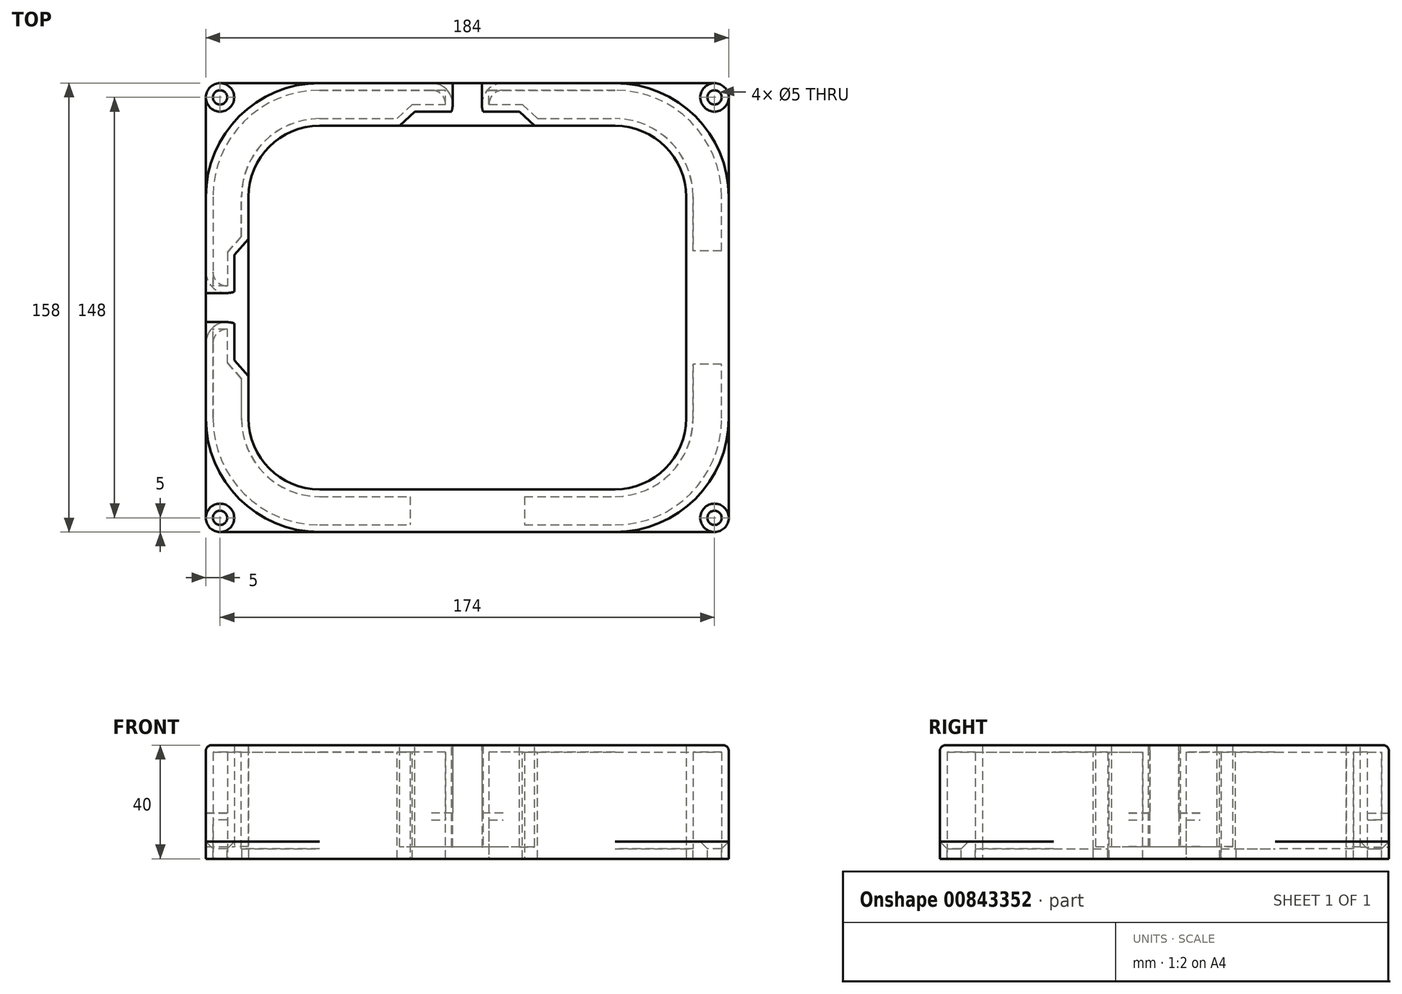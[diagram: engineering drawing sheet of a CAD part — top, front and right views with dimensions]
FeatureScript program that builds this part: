
annotation { "Feature Type Name" : "Feature", "Feature Type Description" : "" }
export const myFeature = defineFeature(function(context is Context, id is Id, definition is map)
    precondition{}
    {
        {
            var Q0;
            Q0=qCreatedBy(makeId("Top.planeOp"),FACE);
            var sketch = newSketch(context, id + "F0", { "sketchPlane" : qUnion([Q0])});
            skLineSegment(sketch, "E0.bottom", {"start": v(-51.5, 63.5) * mm, "end": v(51.5, 63.5) * mm});
            skLineSegment(sketch, "E0.top", {"start": v(-51.5, -63.5) * mm, "end": v(51.5, -63.5) * mm});
            skLineSegment(sketch, "E0.left", {"start": v(-76.5, 38.5) * mm, "end": v(-76.5, -38.5) * mm});
            skLineSegment(sketch, "E0.right", {"start": v(76.5, 38.5) * mm, "end": v(76.5, -38.5) * mm});
            skPoint(sketch, "E0.middle", {"position": v(0, 0) * mm});
            skPoint(sketch, "E1.visualSharp", {"position": v(-76.5, 63.5) * mm});
            skArc(sketch, "E1.filletArc", {"start": v(-51.5, 63.5) * mm, "mid": v(-69.18, 56.18) * mm, "end": v(-76.5, 38.5) * mm});
            skPoint(sketch, "E2.visualSharp", {"position": v(76.5, -63.5) * mm});
            skArc(sketch, "E2.filletArc", {"start": v(51.5, -63.5) * mm, "mid": v(69.18, -56.18) * mm, "end": v(76.5, -38.5) * mm});
            skPoint(sketch, "E3.visualSharp", {"position": v(76.5, 63.5) * mm});
            skArc(sketch, "E3.filletArc", {"start": v(76.5, 38.5) * mm, "mid": v(69.18, 56.18) * mm, "end": v(51.5, 63.5) * mm});
            skPoint(sketch, "E4.visualSharp", {"position": v(-76.5, -63.5) * mm});
            skArc(sketch, "E4.filletArc", {"start": v(-76.5, -38.5) * mm, "mid": v(-69.18, -56.18) * mm, "end": v(-51.5, -63.5) * mm});
            skSolve(sketch);
        }
        {
            var Q0;
            Q0 = qSketchRegion(id + "F0", true);
            extrude(context, id + "F1", {"entities" : qUnion([Q0]), "depth" : 5 * mm, "offsetDistance" : 25 * mm});
        }
        {
            var Q0;
            Q0=qCreatedBy(makeId("Top.planeOp"),FACE);
            var sketch = newSketch(context, id + "F2", { "sketchPlane" : qUnion([Q0])});
            skLineSegment(sketch, "E5.bottom", {"start": v(-52, 64) * mm, "end": v(52, 64) * mm});
            skLineSegment(sketch, "E5.top", {"start": v(-52, -64) * mm, "end": v(52, -64) * mm});
            skLineSegment(sketch, "E5.left", {"start": v(-77, 39) * mm, "end": v(-77, -39) * mm});
            skLineSegment(sketch, "E5.right", {"start": v(77, 39) * mm, "end": v(77, -39) * mm});
            skPoint(sketch, "E5.middle", {"position": v(0, 0) * mm});
            skPoint(sketch, "E6.visualSharp", {"position": v(-77, 64) * mm});
            skArc(sketch, "E6.filletArc", {"start": v(-52, 64) * mm, "mid": v(-69.68, 56.68) * mm, "end": v(-77, 39) * mm});
            skPoint(sketch, "E7.visualSharp", {"position": v(77, 64) * mm});
            skArc(sketch, "E7.filletArc", {"start": v(77, 39) * mm, "mid": v(69.68, 56.68) * mm, "end": v(52, 64) * mm});
            skPoint(sketch, "E8.visualSharp", {"position": v(77, -64) * mm});
            skArc(sketch, "E8.filletArc", {"start": v(52, -64) * mm, "mid": v(69.68, -56.68) * mm, "end": v(77, -39) * mm});
            skPoint(sketch, "E9.visualSharp", {"position": v(-77, -64) * mm});
            skArc(sketch, "E9.filletArc", {"start": v(-77, -39) * mm, "mid": v(-69.68, -56.68) * mm, "end": v(-52, -64) * mm});
            skArc(sketch, "E10.0", {"start": v(-52, 79) * mm, "mid": v(-80.28, 67.28) * mm, "end": v(-92, 39) * mm});
            skLineSegment(sketch, "E10.1", {"start": v(-92, 39) * mm, "end": v(-92, -39) * mm});
            skLineSegment(sketch, "E10.2", {"start": v(-52, 79) * mm, "end": v(52, 79) * mm});
            skArc(sketch, "E10.3", {"start": v(-92, -39) * mm, "mid": v(-80.28, -67.28) * mm, "end": v(-52, -79) * mm});
            skArc(sketch, "E10.4", {"start": v(92, 39) * mm, "mid": v(80.28, 67.28) * mm, "end": v(52, 79) * mm});
            skLineSegment(sketch, "E10.5", {"start": v(92, 39) * mm, "end": v(92, -39) * mm});
            skArc(sketch, "E10.6", {"start": v(52, -79) * mm, "mid": v(80.28, -67.28) * mm, "end": v(92, -39) * mm});
            skLineSegment(sketch, "E10.7", {"start": v(-52, -79) * mm, "end": v(52, -79) * mm});
            skSolve(sketch);
        }
        {
            var Q0;
            Q0 = qSketchRegion(id + "F2", true);
            extrude(context, id + "F3", {"entities" : qUnion([Q0]), "depth" : 40 * mm, "offsetDistance" : 25 * mm});
        }
        {
            var Q0;
            Q0=makeQuery(id+"F3.opExtrude","CAP_FACE",FACE,{"disambiguationData":[OSD([sQuery(id+"F2.wireOp",EDGE,"E5.bottom"),sQuery(id+"F2.wireOp",EDGE,"E5.top"),sQuery(id+"F2.wireOp",EDGE,"E5.left"),sQuery(id+"F2.wireOp",EDGE,"E5.right"),sQuery(id+"F2.wireOp",EDGE,"E6.filletArc"),sQuery(id+"F2.wireOp",EDGE,"E7.filletArc"),sQuery(id+"F2.wireOp",EDGE,"E8.filletArc"),sQuery(id+"F2.wireOp",EDGE,"E9.filletArc"),sQuery(id+"F2.wireOp",EDGE,"E10.0"),sQuery(id+"F2.wireOp",EDGE,"E10.1"),sQuery(id+"F2.wireOp",EDGE,"E10.2"),sQuery(id+"F2.wireOp",EDGE,"E10.3"),sQuery(id+"F2.wireOp",EDGE,"E10.4"),sQuery(id+"F2.wireOp",EDGE,"E10.5"),sQuery(id+"F2.wireOp",EDGE,"E10.6"),sQuery(id+"F2.wireOp",EDGE,"E10.7")])],"isStart":true});
            var sketch = newSketch(context, id + "F4", { "sketchPlane" : qUnion([Q0])});
            skLineSegment(sketch, "E11.bottom", {"start": v(-87, 79) * mm, "end": v(87, 79) * mm});
            skLineSegment(sketch, "E11.top", {"start": v(-87, -79) * mm, "end": v(87, -79) * mm});
            skLineSegment(sketch, "E11.left", {"start": v(-92, 74) * mm, "end": v(-92, -74) * mm});
            skLineSegment(sketch, "E11.right", {"start": v(92, 74) * mm, "end": v(92, -74) * mm});
            skPoint(sketch, "E11.middle", {"position": v(0, 0) * mm});
            skPoint(sketch, "E12.visualSharp", {"position": v(-92, 79) * mm});
            skArc(sketch, "E12.filletArc", {"start": v(-87, 79) * mm, "mid": v(-90.54, 77.54) * mm, "end": v(-92, 74) * mm});
            skPoint(sketch, "E13.visualSharp", {"position": v(92, 79) * mm});
            skArc(sketch, "E13.filletArc", {"start": v(92, 74) * mm, "mid": v(90.54, 77.54) * mm, "end": v(87, 79) * mm});
            skPoint(sketch, "E14.visualSharp", {"position": v(92, -79) * mm});
            skArc(sketch, "E14.filletArc", {"start": v(87, -79) * mm, "mid": v(90.54, -77.54) * mm, "end": v(92, -74) * mm});
            skPoint(sketch, "E15.visualSharp", {"position": v(-92, -79) * mm});
            skArc(sketch, "E15.filletArc", {"start": v(-92, -74) * mm, "mid": v(-90.54, -77.54) * mm, "end": v(-87, -79) * mm});
            skLineSegment(sketch, "E16.bottom", {"start": v(-51.94, 64) * mm, "end": v(51.94, 64) * mm});
            skLineSegment(sketch, "E16.top", {"start": v(-51.94, -64) * mm, "end": v(51.94, -64) * mm});
            skLineSegment(sketch, "E16.left", {"start": v(-76.94, 39) * mm, "end": v(-76.94, -39) * mm});
            skLineSegment(sketch, "E16.right", {"start": v(76.94, 39) * mm, "end": v(76.94, -39) * mm});
            skPoint(sketch, "E17.visualSharp", {"position": v(-76.94, 64) * mm});
            skArc(sketch, "E17.filletArc", {"start": v(-51.94, 64) * mm, "mid": v(-69.61, 56.68) * mm, "end": v(-76.94, 39) * mm});
            skPoint(sketch, "E18.visualSharp", {"position": v(76.94, 64) * mm});
            skArc(sketch, "E18.filletArc", {"start": v(76.94, 39) * mm, "mid": v(69.61, 56.68) * mm, "end": v(51.94, 64) * mm});
            skPoint(sketch, "E19.visualSharp", {"position": v(-76.94, -64) * mm});
            skArc(sketch, "E19.filletArc", {"start": v(-76.94, -39) * mm, "mid": v(-69.61, -56.68) * mm, "end": v(-51.94, -64) * mm});
            skPoint(sketch, "E20.visualSharp", {"position": v(76.94, -64) * mm});
            skArc(sketch, "E20.filletArc", {"start": v(51.94, -64) * mm, "mid": v(69.61, -56.68) * mm, "end": v(76.94, -39) * mm});
            skSolve(sketch);
        }
        {
            var Q0;
            Q0 = qSketchRegion(id + "F4", true);
            extrude(context, id + "F5", {"entities" : qUnion([Q0]), "oppositeDirection" : true, "depth" : 6 * mm, "offsetDistance" : 25 * mm});
        }
        {
            var Q0;
            Q0=makeQuery(id+"F5.opExtrude","CAP_FACE",FACE,{"disambiguationData":[OSD([sQuery(id+"F4.wireOp",EDGE,"E11.bottom"),sQuery(id+"F4.wireOp",EDGE,"E11.top"),sQuery(id+"F4.wireOp",EDGE,"E11.left"),sQuery(id+"F4.wireOp",EDGE,"E11.right"),sQuery(id+"F4.wireOp",EDGE,"E12.filletArc"),sQuery(id+"F4.wireOp",EDGE,"E13.filletArc"),sQuery(id+"F4.wireOp",EDGE,"E14.filletArc"),sQuery(id+"F4.wireOp",EDGE,"E15.filletArc"),sQuery(id+"F4.wireOp",EDGE,"E16.bottom"),sQuery(id+"F4.wireOp",EDGE,"E16.top"),sQuery(id+"F4.wireOp",EDGE,"E16.left"),sQuery(id+"F4.wireOp",EDGE,"E16.right"),sQuery(id+"F4.wireOp",EDGE,"E17.filletArc"),sQuery(id+"F4.wireOp",EDGE,"E18.filletArc"),sQuery(id+"F4.wireOp",EDGE,"E19.filletArc"),sQuery(id+"F4.wireOp",EDGE,"E20.filletArc")])],"isStart":false});
            var sketch = newSketch(context, id + "F6", { "sketchPlane" : qUnion([Q0])});
            skPoint(sketch, "E21", {"position": v(-87, -74) * mm});
            skPoint(sketch, "E22", {"position": v(-87, 74) * mm});
            skPoint(sketch, "E23", {"position": v(87, 74) * mm});
            skPoint(sketch, "E24", {"position": v(87, -74) * mm});
            skSolve(sketch);
        }
        {
            var Q0;
            Q0=sQuery(id+"F6.wireOp",VERTEX,"E24");
            var Q1;
            Q1=sQuery(id+"F6.wireOp",VERTEX,"E21");
            var Q2;
            Q2=sQuery(id+"F6.wireOp",VERTEX,"E22");
            var Q3;
            Q3=sQuery(id+"F6.wireOp",VERTEX,"E23");
            var Q4;
            Q4=makeQuery(id+"F5.opExtrude","SWEPT_BODY",BODY,{"disambiguationData":[OSD([sQuery(id+"F4.wireOp",EDGE,"E11.bottom"),sQuery(id+"F4.wireOp",EDGE,"E11.top"),sQuery(id+"F4.wireOp",EDGE,"E11.left"),sQuery(id+"F4.wireOp",EDGE,"E11.right"),sQuery(id+"F4.wireOp",EDGE,"E12.filletArc"),sQuery(id+"F4.wireOp",EDGE,"E13.filletArc"),sQuery(id+"F4.wireOp",EDGE,"E14.filletArc"),sQuery(id+"F4.wireOp",EDGE,"E15.filletArc"),sQuery(id+"F4.wireOp",EDGE,"E16.bottom"),sQuery(id+"F4.wireOp",EDGE,"E16.top"),sQuery(id+"F4.wireOp",EDGE,"E16.left"),sQuery(id+"F4.wireOp",EDGE,"E16.right"),sQuery(id+"F4.wireOp",EDGE,"E17.filletArc"),sQuery(id+"F4.wireOp",EDGE,"E18.filletArc"),sQuery(id+"F4.wireOp",EDGE,"E19.filletArc"),sQuery(id+"F4.wireOp",EDGE,"E20.filletArc")])]});
            hole(context, id + "F7", {"style" : HoleStyle.C_SINK, "endStyle" : HoleEndStyle.THROUGH, "standardTappedOrClearance" : lookupTablePath({ "standard" : "ISO", "size" : "5", "type" : "Drilled" }), "standardBlindInLast" : lookupTablePath({ "standard" : "ISO", "size" : "5", "type" : "Drilled" }), "holeDiameter" : 5 * mm, "cSinkDiameter" : 10 * mm, "cSinkAngle" : 90 * degree, "majorDiameter" : 5 * mm, "isTappedThrough" : true, "tappedDepth" : 12 * mm, "tapClearance" : 3, "locations" : qUnion([Q0, Q1, Q2, Q3]), "scope" : qUnion([Q4])});
        }
        {
            var Q0;
            Q0=makeQuery(id+"F3.opExtrude","SWEPT_FACE",FACE,{"disambiguationData":[OSD([sQuery(id+"F2.wireOp",EDGE,"E10.1")])]});
            var sketch = newSketch(context, id + "F8", { "sketchPlane" : qUnion([Q0])});
            skLineSegment(sketch, "E25", {"start": v(0, 40) * mm, "end": v(0, 16.12) * mm});
            skLineSegment(sketch, "E26.bottom", {"start": v(-5.13, 40) * mm, "end": v(5.13, 40) * mm});
            skLineSegment(sketch, "E26.top", {"start": v(-5.13, 16.12) * mm, "end": v(5.13, 16.12) * mm});
            skLineSegment(sketch, "E26.left", {"start": v(-5.13, 40) * mm, "end": v(-5.13, 16.12) * mm});
            skLineSegment(sketch, "E26.right", {"start": v(5.13, 40) * mm, "end": v(5.13, 16.12) * mm});
            skPoint(sketch, "E26.middle", {"position": v(0, 28.06) * mm});
            skSolve(sketch);
        }
        {
            var Q0;
            Q0 = qSketchRegion(id + "F8", true);
            extrude(context, id + "F9", {"entities" : qUnion([Q0]), "operationType" : NewBodyOperationType.REMOVE, "oppositeDirection" : true, "depth" : 25 * mm, "offsetDistance" : 25 * mm});
        }
        {
            var Q0;
            Q0=makeQuery(id+"F3.opExtrude","SWEPT_FACE",FACE,{"disambiguationData":[OSD([sQuery(id+"F2.wireOp",EDGE,"E10.2")])]});
            var sketch = newSketch(context, id + "F10", { "sketchPlane" : qUnion([Q0])});
            skLineSegment(sketch, "E27", {"start": v(0, 40) * mm, "end": v(0, 16.14) * mm});
            skLineSegment(sketch, "E28.bottom", {"start": v(-5.13, 40) * mm, "end": v(5.13, 40) * mm});
            skLineSegment(sketch, "E28.top", {"start": v(-5.13, 16.14) * mm, "end": v(5.13, 16.14) * mm});
            skLineSegment(sketch, "E28.left", {"start": v(-5.13, 40) * mm, "end": v(-5.13, 16.14) * mm});
            skLineSegment(sketch, "E28.right", {"start": v(5.13, 40) * mm, "end": v(5.13, 16.14) * mm});
            skPoint(sketch, "E28.middle", {"position": v(0, 28.07) * mm});
            skSolve(sketch);
        }
        {
            var Q0;
            Q0 = qSketchRegion(id + "F10", true);
            extrude(context, id + "F11", {"entities" : qUnion([Q0]), "operationType" : NewBodyOperationType.REMOVE, "oppositeDirection" : true, "depth" : 25 * mm, "offsetDistance" : 25 * mm});
        }
        {
            var Q0;
            Q0=makeQuery(id+"F11.boolean.opBoolean","INTERSECT",EDGE,{"derivedFrom":[makeQuery(id+"F3.opExtrude","SWEPT_FACE",FACE,{"disambiguationData":[OSD([sQuery(id+"F2.wireOp",EDGE,"E5.bottom")])]}),makeQuery(id+"F11.opExtrude","SWEPT_FACE",FACE,{"disambiguationData":[OSD([sQuery(id+"F10.wireOp",EDGE,"E28.left")])]})]});
            var Q1;
            Q1=makeQuery(id+"F11.boolean.opBoolean","COPY",EDGE,{"derivedFrom":makeQuery(id+"F11.opExtrude","CAP_EDGE",EDGE,{"disambiguationData":[OSD([sQuery(id+"F10.wireOp",EDGE,"E28.left")])],"isStart":true})});
            var Q2;
            Q2=makeQuery(id+"F11.boolean.opBoolean","COPY",EDGE,{"derivedFrom":makeQuery(id+"F11.opExtrude","CAP_EDGE",EDGE,{"disambiguationData":[OSD([sQuery(id+"F10.wireOp",EDGE,"E28.right")])],"isStart":true})});
            var Q3;
            Q3=makeQuery(id+"F11.boolean.opBoolean","INTERSECT",EDGE,{"derivedFrom":[makeQuery(id+"F3.opExtrude","SWEPT_FACE",FACE,{"disambiguationData":[OSD([sQuery(id+"F2.wireOp",EDGE,"E5.bottom")])]}),makeQuery(id+"F11.opExtrude","SWEPT_FACE",FACE,{"disambiguationData":[OSD([sQuery(id+"F10.wireOp",EDGE,"E28.right")])]})]});
            var Q4;
            Q4=makeQuery(id+"F9.boolean.opBoolean","INTERSECT",EDGE,{"derivedFrom":[makeQuery(id+"F3.opExtrude","SWEPT_FACE",FACE,{"disambiguationData":[OSD([sQuery(id+"F2.wireOp",EDGE,"E5.left")])]}),makeQuery(id+"F9.opExtrude","SWEPT_FACE",FACE,{"disambiguationData":[OSD([sQuery(id+"F8.wireOp",EDGE,"E26.right")])]})]});
            var Q5;
            Q5=makeQuery(id+"F9.boolean.opBoolean","INTERSECT",EDGE,{"derivedFrom":[makeQuery(id+"F3.opExtrude","SWEPT_FACE",FACE,{"disambiguationData":[OSD([sQuery(id+"F2.wireOp",EDGE,"E5.left")])]}),makeQuery(id+"F9.opExtrude","SWEPT_FACE",FACE,{"disambiguationData":[OSD([sQuery(id+"F8.wireOp",EDGE,"E26.left")])]})]});
            var Q6;
            Q6=makeQuery(id+"F9.boolean.opBoolean","COPY",EDGE,{"derivedFrom":makeQuery(id+"F9.opExtrude","CAP_EDGE",EDGE,{"disambiguationData":[OSD([sQuery(id+"F8.wireOp",EDGE,"E26.right")])],"isStart":true})});
            var Q7;
            Q7=makeQuery(id+"F9.boolean.opBoolean","COPY",EDGE,{"derivedFrom":makeQuery(id+"F9.opExtrude","CAP_EDGE",EDGE,{"disambiguationData":[OSD([sQuery(id+"F8.wireOp",EDGE,"E26.left")])],"isStart":true})});
            fillet(context, id + "F12", {"entities" : qUnion([Q0, Q1, Q2, Q3, Q4, Q5, Q6, Q7]), "radius" : 7.5 * mm, "tangentPropagation" : true, "allowEdgeOverflow" : false});
        }
        {
            var Q0;
            Q0=makeQuery(id+"F3.opExtrude","CAP_EDGE",EDGE,{"disambiguationData":[OSD([sQuery(id+"F2.wireOp",EDGE,"E10.0")])],"isStart":false});
            var Q1;
            Q1=makeQuery(id+"F3.opExtrude","CAP_EDGE",EDGE,{"disambiguationData":[OSD([sQuery(id+"F2.wireOp",EDGE,"E10.4")])],"isStart":false});
            fillet(context, id + "F13", {"entities" : qUnion([Q0, Q1]), "radius" : 2 * mm, "tangentPropagation" : true, "allowEdgeOverflow" : false});
        }
        {
            var Q0;
            Q0=makeQuery(id+"F1.opExtrude","SWEPT_BODY",BODY,{"disambiguationData":[OSD([sQuery(id+"F0.wireOp",EDGE,"E0.bottom"),sQuery(id+"F0.wireOp",EDGE,"E0.top"),sQuery(id+"F0.wireOp",EDGE,"E0.left"),sQuery(id+"F0.wireOp",EDGE,"E0.right"),sQuery(id+"F0.wireOp",EDGE,"E1.filletArc"),sQuery(id+"F0.wireOp",EDGE,"E2.filletArc"),sQuery(id+"F0.wireOp",EDGE,"E3.filletArc"),sQuery(id+"F0.wireOp",EDGE,"E4.filletArc")])]});
            deleteBodies(context, id + "F14", {"entities" : qUnion([Q0])});
        }
        {
            var Q0;
            Q0=makeQuery(id+"F3.opExtrude","SWEPT_BODY",BODY,{"disambiguationData":[OSD([sQuery(id+"F2.wireOp",EDGE,"E5.bottom"),sQuery(id+"F2.wireOp",EDGE,"E5.top"),sQuery(id+"F2.wireOp",EDGE,"E5.left"),sQuery(id+"F2.wireOp",EDGE,"E5.right"),sQuery(id+"F2.wireOp",EDGE,"E6.filletArc"),sQuery(id+"F2.wireOp",EDGE,"E7.filletArc"),sQuery(id+"F2.wireOp",EDGE,"E8.filletArc"),sQuery(id+"F2.wireOp",EDGE,"E9.filletArc"),sQuery(id+"F2.wireOp",EDGE,"E10.0"),sQuery(id+"F2.wireOp",EDGE,"E10.1"),sQuery(id+"F2.wireOp",EDGE,"E10.2"),sQuery(id+"F2.wireOp",EDGE,"E10.3"),sQuery(id+"F2.wireOp",EDGE,"E10.4"),sQuery(id+"F2.wireOp",EDGE,"E10.5"),sQuery(id+"F2.wireOp",EDGE,"E10.6"),sQuery(id+"F2.wireOp",EDGE,"E10.7")])]});
            var Q1;
            Q1=makeQuery(id+"F5.opExtrude","SWEPT_BODY",BODY,{"disambiguationData":[OSD([sQuery(id+"F4.wireOp",EDGE,"E11.bottom"),sQuery(id+"F4.wireOp",EDGE,"E11.top"),sQuery(id+"F4.wireOp",EDGE,"E11.left"),sQuery(id+"F4.wireOp",EDGE,"E11.right"),sQuery(id+"F4.wireOp",EDGE,"E12.filletArc"),sQuery(id+"F4.wireOp",EDGE,"E13.filletArc"),sQuery(id+"F4.wireOp",EDGE,"E14.filletArc"),sQuery(id+"F4.wireOp",EDGE,"E15.filletArc"),sQuery(id+"F4.wireOp",EDGE,"E16.bottom"),sQuery(id+"F4.wireOp",EDGE,"E16.top"),sQuery(id+"F4.wireOp",EDGE,"E16.left"),sQuery(id+"F4.wireOp",EDGE,"E16.right"),sQuery(id+"F4.wireOp",EDGE,"E17.filletArc"),sQuery(id+"F4.wireOp",EDGE,"E18.filletArc"),sQuery(id+"F4.wireOp",EDGE,"E19.filletArc"),sQuery(id+"F4.wireOp",EDGE,"E20.filletArc")])]});
            booleanBodies(context, id + "F15", {"operationType" : BooleanOperationType.UNION, "tools" : qUnion([Q0, Q1])});
        }
        {
            var Q0;
            {var subQ0=sQuery(id+"F2.wireOp",EDGE,"E10.3");var subQ1=sQuery(id+"F2.wireOp",EDGE,"E10.2");var subQ2=sQuery(id+"F2.wireOp",EDGE,"E9.filletArc");var subQ3=sQuery(id+"F2.wireOp",EDGE,"E8.filletArc");var subQ4=sQuery(id+"F2.wireOp",EDGE,"E7.filletArc");var subQ5=sQuery(id+"F2.wireOp",EDGE,"E10.1");var subQ6=sQuery(id+"F2.wireOp",EDGE,"E5.bottom");var subQ7=sQuery(id+"F2.wireOp",EDGE,"E5.right");var subQ8=sQuery(id+"F2.wireOp",EDGE,"E5.top");var subQ9=sQuery(id+"F2.wireOp",EDGE,"E5.left");var subQ10=sQuery(id+"F2.wireOp",EDGE,"E10.4");var subQ11=sQuery(id+"F2.wireOp",EDGE,"E10.5");var subQ12=sQuery(id+"F2.wireOp",EDGE,"E10.6");var subQ13=sQuery(id+"F2.wireOp",EDGE,"E10.7");Q0=makeQuery(id+"F11.boolean.opBoolean","SPLIT",FACE,{"disambiguationData":[TD([makeQuery(id+"F3.opExtrude","SWEPT_FACE",FACE,{"disambiguationData":[OSD([subQ8])]})])],"derivedFrom":makeQuery(id+"F3.opExtrude","CAP_FACE",FACE,{"disambiguationData":[OSD([subQ6,subQ8,subQ9,subQ7,sQuery(id+"F2.wireOp",EDGE,"E6.filletArc"),subQ4,subQ3,subQ2,sQuery(id+"F2.wireOp",EDGE,"E10.0"),subQ5,subQ1,subQ0,subQ10,subQ11,subQ12,subQ13])],"isStart":false})});}
            var sketch = newSketch(context, id + "F16", { "sketchPlane" : qUnion([Q0])});
            skLineSegment(sketch, "E29", {"start": v(18.42, 69) * mm, "end": v(23.86, 63.91) * mm});
            skLineSegment(sketch, "E30.MirrorCS", {"start": v(-18.42, 69) * mm, "end": v(-23.86, 63.91) * mm});
            skLineSegment(sketch, "E31", {"start": v(18.42, 69) * mm, "end": v(-18.42, 69) * mm});
            skPoint(sketch, "E32.end.orphan", {"position": v(0, 64) * mm});
            skLineSegment(sketch, "E33", {"start": v(23.86, 63.91) * mm, "end": v(-23.86, 63.91) * mm});
            skSolve(sketch);
        }
        {
            var Q0;
            Q0 = qSketchRegion(id + "F16", true);
            var Q1;
            Q1=makeQuery(id+"F11.boolean.opBoolean","COPY",FACE,{"derivedFrom":makeQuery(id+"F11.opExtrude","SWEPT_FACE",FACE,{"disambiguationData":[OSD([sQuery(id+"F10.wireOp",EDGE,"E28.top")])]})});
            extrude(context, id + "F17", {"entities" : qUnion([Q0]), "operationType" : NewBodyOperationType.REMOVE, "endBound" : BoundingType.UP_TO_SURFACE, "oppositeDirection" : true, "depth" : 25 * mm, "endBoundEntityFace" : qUnion([Q1]), "offsetDistance" : 25 * mm});
        }
        {
            var Q0;
            {var subQ0=sQuery(id+"F2.wireOp",EDGE,"E6.filletArc");var subQ1=sQuery(id+"F2.wireOp",EDGE,"E5.left");var subQ2=sQuery(id+"F2.wireOp",EDGE,"E10.0");var subQ3=sQuery(id+"F2.wireOp",EDGE,"E5.bottom");var subQ4=sQuery(id+"F2.wireOp",EDGE,"E10.1");var subQ5=sQuery(id+"F2.wireOp",EDGE,"E10.2");Q0=makeQuery(id+"F11.boolean.opBoolean","SPLIT",FACE,{"disambiguationData":[TD([makeQuery(id+"F3.opExtrude","SWEPT_FACE",FACE,{"disambiguationData":[OSD([subQ0])]})])],"derivedFrom":makeQuery(id+"F3.opExtrude","CAP_FACE",FACE,{"disambiguationData":[OSD([subQ3,sQuery(id+"F2.wireOp",EDGE,"E5.top"),subQ1,sQuery(id+"F2.wireOp",EDGE,"E5.right"),subQ0,sQuery(id+"F2.wireOp",EDGE,"E7.filletArc"),sQuery(id+"F2.wireOp",EDGE,"E8.filletArc"),sQuery(id+"F2.wireOp",EDGE,"E9.filletArc"),subQ2,subQ4,subQ5,sQuery(id+"F2.wireOp",EDGE,"E10.3"),sQuery(id+"F2.wireOp",EDGE,"E10.4"),sQuery(id+"F2.wireOp",EDGE,"E10.5"),sQuery(id+"F2.wireOp",EDGE,"E10.6"),sQuery(id+"F2.wireOp",EDGE,"E10.7")])],"isStart":false})});}
            var sketch = newSketch(context, id + "F18", { "sketchPlane" : qUnion([Q0])});
            skLineSegment(sketch, "E34", {"start": v(-76.94, 24.15) * mm, "end": v(-81.94, 18.5) * mm});
            skLineSegment(sketch, "E35.MirrorCS", {"start": v(-76.94, -24.15) * mm, "end": v(-81.94, -18.5) * mm});
            skLineSegment(sketch, "E36", {"start": v(-81.94, -18.5) * mm, "end": v(-81.94, 18.5) * mm});
            skPoint(sketch, "E37.start.orphan", {"position": v(-77.1, 0) * mm});
            skLineSegment(sketch, "E38", {"start": v(-76.94, 24.15) * mm, "end": v(-76.94, -24.15) * mm});
            skSolve(sketch);
        }
        {
            var Q0;
            Q0 = qSketchRegion(id + "F18", true);
            var Q1;
            Q1=makeQuery(id+"F9.boolean.opBoolean","COPY",FACE,{"derivedFrom":makeQuery(id+"F9.opExtrude","SWEPT_FACE",FACE,{"disambiguationData":[OSD([sQuery(id+"F8.wireOp",EDGE,"E26.top")])]})});
            extrude(context, id + "F19", {"entities" : qUnion([Q0]), "operationType" : NewBodyOperationType.REMOVE, "endBound" : BoundingType.UP_TO_SURFACE, "oppositeDirection" : true, "depth" : 25 * mm, "endBoundEntityFace" : qUnion([Q1]), "offsetDistance" : 25 * mm});
        }
        {
            var Q0;
            Q0=makeQuery(id+"F15.opBoolean","MERGE",FACE,{"derivedFrom":[makeQuery(id+"F3.opExtrude","CAP_FACE",FACE,{"disambiguationData":[OSD([sQuery(id+"F2.wireOp",EDGE,"E5.bottom"),sQuery(id+"F2.wireOp",EDGE,"E5.top"),sQuery(id+"F2.wireOp",EDGE,"E5.left"),sQuery(id+"F2.wireOp",EDGE,"E5.right"),sQuery(id+"F2.wireOp",EDGE,"E6.filletArc"),sQuery(id+"F2.wireOp",EDGE,"E7.filletArc"),sQuery(id+"F2.wireOp",EDGE,"E8.filletArc"),sQuery(id+"F2.wireOp",EDGE,"E9.filletArc"),sQuery(id+"F2.wireOp",EDGE,"E10.0"),sQuery(id+"F2.wireOp",EDGE,"E10.1"),sQuery(id+"F2.wireOp",EDGE,"E10.2"),sQuery(id+"F2.wireOp",EDGE,"E10.3"),sQuery(id+"F2.wireOp",EDGE,"E10.4"),sQuery(id+"F2.wireOp",EDGE,"E10.5"),sQuery(id+"F2.wireOp",EDGE,"E10.6"),sQuery(id+"F2.wireOp",EDGE,"E10.7")])],"isStart":true}),makeQuery(id+"F5.opExtrude","CAP_FACE",FACE,{"disambiguationData":[OSD([sQuery(id+"F4.wireOp",EDGE,"E11.bottom"),sQuery(id+"F4.wireOp",EDGE,"E11.top"),sQuery(id+"F4.wireOp",EDGE,"E11.left"),sQuery(id+"F4.wireOp",EDGE,"E11.right"),sQuery(id+"F4.wireOp",EDGE,"E12.filletArc"),sQuery(id+"F4.wireOp",EDGE,"E13.filletArc"),sQuery(id+"F4.wireOp",EDGE,"E14.filletArc"),sQuery(id+"F4.wireOp",EDGE,"E15.filletArc"),sQuery(id+"F4.wireOp",EDGE,"E16.bottom"),sQuery(id+"F4.wireOp",EDGE,"E16.top"),sQuery(id+"F4.wireOp",EDGE,"E16.left"),sQuery(id+"F4.wireOp",EDGE,"E16.right"),sQuery(id+"F4.wireOp",EDGE,"E17.filletArc"),sQuery(id+"F4.wireOp",EDGE,"E18.filletArc"),sQuery(id+"F4.wireOp",EDGE,"E19.filletArc"),sQuery(id+"F4.wireOp",EDGE,"E20.filletArc")])],"isStart":true})]});
            shell(context, id + "F20", {"entities" : qUnion([Q0]), "thickness" : 2.5 * mm});
        }
        {
            var Q0;
            {var subQ0=sQuery(id+"F4.wireOp",EDGE,"E11.top");var subQ1=sQuery(id+"F4.wireOp",EDGE,"E11.right");var subQ2=sQuery(id+"F4.wireOp",EDGE,"E14.filletArc");var subQ3=sQuery(id+"F4.wireOp",EDGE,"E20.filletArc");var subQ4=sQuery(id+"F4.wireOp",EDGE,"E19.filletArc");var subQ5=sQuery(id+"F4.wireOp",EDGE,"E18.filletArc");var subQ6=sQuery(id+"F4.wireOp",EDGE,"E17.filletArc");var subQ7=sQuery(id+"F4.wireOp",EDGE,"E16.right");var subQ8=sQuery(id+"F4.wireOp",EDGE,"E16.left");var subQ9=sQuery(id+"F4.wireOp",EDGE,"E16.top");var subQ10=sQuery(id+"F4.wireOp",EDGE,"E16.bottom");var subQ11=sQuery(id+"F4.wireOp",EDGE,"E15.filletArc");var subQ12=sQuery(id+"F4.wireOp",EDGE,"E13.filletArc");var subQ13=sQuery(id+"F4.wireOp",EDGE,"E12.filletArc");var subQ14=sQuery(id+"F4.wireOp",EDGE,"E11.left");var subQ15=sQuery(id+"F4.wireOp",EDGE,"E11.bottom");Q0=makeQuery(id+"F20.opShell","OFFSET_FACE",FACE,{"disambiguationData":[OSD([subQ15,subQ0,subQ14,subQ1,subQ13,subQ12,subQ2,subQ11,subQ10,subQ9,subQ8,subQ7,subQ6,subQ5,subQ4,subQ3]),TDD([makeQuery(id+"F15.opBoolean","SPLIT",FACE,{"disambiguationData":[TD([makeQuery(id+"F3.opExtrude","SWEPT_FACE",FACE,{"disambiguationData":[OSD([sQuery(id+"F2.wireOp",EDGE,"E10.4")])]})])],"derivedFrom":makeQuery(id+"F5.opExtrude","CAP_FACE",FACE,{"disambiguationData":[OSD([subQ15,subQ0,subQ14,subQ1,subQ13,subQ12,subQ2,subQ11,subQ10,subQ9,subQ8,subQ7,subQ6,subQ5,subQ4,subQ3])],"isStart":false})})])]});}
            var sketch = newSketch(context, id + "F21", { "sketchPlane" : qUnion([Q0])});
            skArc(sketch, "E39", {"start": v(52, -76.5) * mm, "mid": v(78.52, -65.52) * mm, "end": v(89.5, -39) * mm});
            skArc(sketch, "E40", {"start": v(89.5, -70.08) * mm, "mid": v(83.71, -70.71) * mm, "end": v(83.08, -76.5) * mm});
            skLineSegment(sketch, "E41", {"start": v(52, -76.5) * mm, "end": v(83.08, -76.5) * mm});
            skLineSegment(sketch, "E42", {"start": v(89.5, -70.08) * mm, "end": v(89.5, -39) * mm});
            skPoint(sketch, "E43.orphan", {"position": v(89.5, -70.94) * mm});
            skLineSegment(sketch, "E44", {"start": v(0, 0) * mm, "end": v(0, -36.63) * mm});
            skPoint(sketch, "E45.MirrorP", {"position": v(-89.5, -70.94) * mm});
            skLineSegment(sketch, "E46.MirrorCS", {"start": v(-52, -76.5) * mm, "end": v(-83.08, -76.5) * mm});
            skArc(sketch, "E47.MirrorCS", {"start": v(-89.5, -70.08) * mm, "mid": v(-83.71, -70.71) * mm, "end": v(-83.08, -76.5) * mm});
            skArc(sketch, "E48.MirrorCS", {"start": v(-52, -76.5) * mm, "mid": v(-78.52, -65.52) * mm, "end": v(-89.5, -39) * mm});
            skLineSegment(sketch, "E49.MirrorCS", {"start": v(-89.5, -70.08) * mm, "end": v(-89.5, -39) * mm});
            skLineSegment(sketch, "E50", {"start": v(0, 0) * mm, "end": v(23.37, 0) * mm});
            skArc(sketch, "E51.MirrorCS", {"start": v(-52, 76.5) * mm, "mid": v(-78.52, 65.52) * mm, "end": v(-89.5, 39) * mm});
            skLineSegment(sketch, "E52.MirrorCS", {"start": v(-89.5, 70.08) * mm, "end": v(-89.5, 39) * mm});
            skArc(sketch, "E53.MirrorCS", {"start": v(-89.5, 70.08) * mm, "mid": v(-83.71, 70.71) * mm, "end": v(-83.08, 76.5) * mm});
            skLineSegment(sketch, "E54.MirrorCS", {"start": v(-52, 76.5) * mm, "end": v(-83.08, 76.5) * mm});
            skLineSegment(sketch, "E55.MirrorCS", {"start": v(89.5, 70.08) * mm, "end": v(89.5, 39) * mm});
            skPoint(sketch, "E56.MirrorP", {"position": v(-89.5, 70.94) * mm});
            skArc(sketch, "E57.MirrorCS", {"start": v(52, 76.5) * mm, "mid": v(78.52, 65.52) * mm, "end": v(89.5, 39) * mm});
            skPoint(sketch, "E58.MirrorP", {"position": v(89.5, 70.94) * mm});
            skLineSegment(sketch, "E59.MirrorCS", {"start": v(52, 76.5) * mm, "end": v(83.08, 76.5) * mm});
            skArc(sketch, "E60.MirrorCS", {"start": v(89.5, 70.08) * mm, "mid": v(83.71, 70.71) * mm, "end": v(83.08, 76.5) * mm});
            skSolve(sketch);
        }
        {
            var Q0;
            Q0 = qSketchRegion(id + "F21", true);
            var Q1;
            Q1=makeQuery(id+"F20.opShell","OFFSET_FACE",FACE,{"disambiguationData":[OSD([sQuery(id+"F2.wireOp",EDGE,"E5.bottom"),sQuery(id+"F2.wireOp",EDGE,"E5.top"),sQuery(id+"F2.wireOp",EDGE,"E5.left"),sQuery(id+"F2.wireOp",EDGE,"E5.right"),sQuery(id+"F2.wireOp",EDGE,"E6.filletArc"),sQuery(id+"F2.wireOp",EDGE,"E7.filletArc"),sQuery(id+"F2.wireOp",EDGE,"E8.filletArc"),sQuery(id+"F2.wireOp",EDGE,"E9.filletArc"),sQuery(id+"F2.wireOp",EDGE,"E10.0"),sQuery(id+"F2.wireOp",EDGE,"E10.1"),sQuery(id+"F2.wireOp",EDGE,"E10.2"),sQuery(id+"F2.wireOp",EDGE,"E10.3"),sQuery(id+"F2.wireOp",EDGE,"E10.4"),sQuery(id+"F2.wireOp",EDGE,"E10.5"),sQuery(id+"F2.wireOp",EDGE,"E10.6"),sQuery(id+"F2.wireOp",EDGE,"E10.7"),sQuery(id+"F4.wireOp",EDGE,"E11.bottom"),sQuery(id+"F4.wireOp",EDGE,"E11.top"),sQuery(id+"F4.wireOp",EDGE,"E11.left"),sQuery(id+"F4.wireOp",EDGE,"E11.right"),sQuery(id+"F4.wireOp",EDGE,"E12.filletArc"),sQuery(id+"F4.wireOp",EDGE,"E13.filletArc"),sQuery(id+"F4.wireOp",EDGE,"E14.filletArc"),sQuery(id+"F4.wireOp",EDGE,"E15.filletArc"),sQuery(id+"F4.wireOp",EDGE,"E16.bottom"),sQuery(id+"F4.wireOp",EDGE,"E16.top"),sQuery(id+"F4.wireOp",EDGE,"E16.left"),sQuery(id+"F4.wireOp",EDGE,"E16.right"),sQuery(id+"F4.wireOp",EDGE,"E17.filletArc"),sQuery(id+"F4.wireOp",EDGE,"E18.filletArc"),sQuery(id+"F4.wireOp",EDGE,"E19.filletArc"),sQuery(id+"F4.wireOp",EDGE,"E20.filletArc")])]});
            extrude(context, id + "F22", {"entities" : qUnion([Q0]), "operationType" : NewBodyOperationType.ADD, "endBound" : BoundingType.UP_TO_SURFACE, "depth" : 25 * mm, "endBoundEntityFace" : qUnion([Q1]), "offsetDistance" : 25 * mm});
        }
        {
            var Q0;
            Q0=makeQuery(id+"F20.opShell","OFFSET_FACE",FACE,{"disambiguationData":[OSD([sQuery(id+"F10.wireOp",EDGE,"E28.top")])]});
            var sketch = newSketch(context, id + "F23", { "sketchPlane" : qUnion([Q0])});
            skArc(sketch, "E61", {"start": v(7.63, -71.5) * mm, "mid": v(9.1, -75.03) * mm, "end": v(12.63, -76.5) * mm});
            skArc(sketch, "E62", {"start": v(-12.63, -76.5) * mm, "mid": v(-9.1, -75.03) * mm, "end": v(-7.63, -71.5) * mm});
            skLineSegment(sketch, "E63", {"start": v(-12.63, -76.5) * mm, "end": v(12.63, -76.5) * mm});
            skLineSegment(sketch, "E64", {"start": v(-7.63, -71.5) * mm, "end": v(-19.4, -71.5) * mm});
            skLineSegment(sketch, "E65", {"start": v(-19.4, -71.5) * mm, "end": v(-24.75, -66.5) * mm});
            skLineSegment(sketch, "E66", {"start": v(-24.75, -66.5) * mm, "end": v(24.75, -66.5) * mm});
            skLineSegment(sketch, "E67", {"start": v(24.75, -66.5) * mm, "end": v(19.4, -71.5) * mm});
            skLineSegment(sketch, "E68", {"start": v(19.4, -71.5) * mm, "end": v(7.63, -71.5) * mm});
            skSolve(sketch);
        }
        {
            var Q0;
            Q0 = qSketchRegion(id + "F23", true);
            var Q1;
            Q1=makeQuery(id+"F22.boolean.opBoolean","MERGE",FACE,{"derivedFrom":[makeQuery(id+"F20.opShell","OFFSET_FACE",FACE,{"disambiguationData":[OSD([sQuery(id+"F2.wireOp",EDGE,"E5.bottom"),sQuery(id+"F2.wireOp",EDGE,"E5.top"),sQuery(id+"F2.wireOp",EDGE,"E5.left"),sQuery(id+"F2.wireOp",EDGE,"E5.right"),sQuery(id+"F2.wireOp",EDGE,"E6.filletArc"),sQuery(id+"F2.wireOp",EDGE,"E7.filletArc"),sQuery(id+"F2.wireOp",EDGE,"E8.filletArc"),sQuery(id+"F2.wireOp",EDGE,"E9.filletArc"),sQuery(id+"F2.wireOp",EDGE,"E10.0"),sQuery(id+"F2.wireOp",EDGE,"E10.1"),sQuery(id+"F2.wireOp",EDGE,"E10.2"),sQuery(id+"F2.wireOp",EDGE,"E10.3"),sQuery(id+"F2.wireOp",EDGE,"E10.4"),sQuery(id+"F2.wireOp",EDGE,"E10.5"),sQuery(id+"F2.wireOp",EDGE,"E10.6"),sQuery(id+"F2.wireOp",EDGE,"E10.7"),sQuery(id+"F4.wireOp",EDGE,"E11.bottom"),sQuery(id+"F4.wireOp",EDGE,"E11.top"),sQuery(id+"F4.wireOp",EDGE,"E11.left"),sQuery(id+"F4.wireOp",EDGE,"E11.right"),sQuery(id+"F4.wireOp",EDGE,"E12.filletArc"),sQuery(id+"F4.wireOp",EDGE,"E13.filletArc"),sQuery(id+"F4.wireOp",EDGE,"E14.filletArc"),sQuery(id+"F4.wireOp",EDGE,"E15.filletArc"),sQuery(id+"F4.wireOp",EDGE,"E16.bottom"),sQuery(id+"F4.wireOp",EDGE,"E16.top"),sQuery(id+"F4.wireOp",EDGE,"E16.left"),sQuery(id+"F4.wireOp",EDGE,"E16.right"),sQuery(id+"F4.wireOp",EDGE,"E17.filletArc"),sQuery(id+"F4.wireOp",EDGE,"E18.filletArc"),sQuery(id+"F4.wireOp",EDGE,"E19.filletArc"),sQuery(id+"F4.wireOp",EDGE,"E20.filletArc")])]}),makeQuery(id+"F22.opExtrude","CAP_FACE",FACE,{"disambiguationData":[OSD([sQuery(id+"F21.wireOp",EDGE,"E39"),sQuery(id+"F21.wireOp",EDGE,"E40"),sQuery(id+"F21.wireOp",EDGE,"E41"),sQuery(id+"F21.wireOp",EDGE,"E42")])],"isStart":false}),makeQuery(id+"F22.opExtrude","CAP_FACE",FACE,{"disambiguationData":[OSD([sQuery(id+"F21.wireOp",EDGE,"E46.MirrorCS"),sQuery(id+"F21.wireOp",EDGE,"E47.MirrorCS"),sQuery(id+"F21.wireOp",EDGE,"E49.MirrorCS"),sQuery(id+"F21.wireOp",EDGE,"E48.MirrorCS")])],"isStart":false}),makeQuery(id+"F22.opExtrude","CAP_FACE",FACE,{"disambiguationData":[OSD([sQuery(id+"F21.wireOp",EDGE,"E52.MirrorCS"),sQuery(id+"F21.wireOp",EDGE,"E53.MirrorCS"),sQuery(id+"F21.wireOp",EDGE,"E51.MirrorCS"),sQuery(id+"F21.wireOp",EDGE,"E54.MirrorCS")])],"isStart":false}),makeQuery(id+"F22.opExtrude","CAP_FACE",FACE,{"disambiguationData":[OSD([sQuery(id+"F21.wireOp",EDGE,"E55.MirrorCS"),sQuery(id+"F21.wireOp",EDGE,"E57.MirrorCS"),sQuery(id+"F21.wireOp",EDGE,"E59.MirrorCS"),sQuery(id+"F21.wireOp",EDGE,"E60.MirrorCS")])],"isStart":false})]});
            extrude(context, id + "F24", {"entities" : qUnion([Q0]), "operationType" : NewBodyOperationType.ADD, "endBound" : BoundingType.UP_TO_SURFACE, "depth" : 25 * mm, "endBoundEntityFace" : qUnion([Q1]), "offsetDistance" : 25 * mm});
        }
        {
            var Q0;
            Q0=makeQuery(id+"F20.opShell","OFFSET_FACE",FACE,{"disambiguationData":[OSD([sQuery(id+"F8.wireOp",EDGE,"E26.top")])]});
            var sketch = newSketch(context, id + "F25", { "sketchPlane" : qUnion([Q0])});
            skArc(sketch, "E69", {"start": v(-89.5, 12.63) * mm, "mid": v(-88.01, 9.07) * mm, "end": v(-84.44, 7.63) * mm});
            skArc(sketch, "E70", {"start": v(-84.44, -7.63) * mm, "mid": v(-88.01, -9.07) * mm, "end": v(-89.5, -12.63) * mm});
            skLineSegment(sketch, "E71", {"start": v(-89.5, 12.63) * mm, "end": v(-89.5, -12.63) * mm});
            skLineSegment(sketch, "E72", {"start": v(-84.44, -7.63) * mm, "end": v(-84.44, -19.45) * mm});
            skLineSegment(sketch, "E73", {"start": v(-84.44, -19.45) * mm, "end": v(-79.5, -25.03) * mm});
            skLineSegment(sketch, "E74", {"start": v(-79.5, -25.03) * mm, "end": v(-79.5, 25.03) * mm});
            skLineSegment(sketch, "E75", {"start": v(-79.5, 25.03) * mm, "end": v(-84.44, 19.45) * mm});
            skLineSegment(sketch, "E76", {"start": v(-84.44, 19.45) * mm, "end": v(-84.44, 7.63) * mm});
            skSolve(sketch);
        }
        {
            var Q0;
            Q0 = qSketchRegion(id + "F25", true);
            var Q1;
            {var subQ0=sQuery(id+"F4.wireOp",EDGE,"E20.filletArc");var subQ1=sQuery(id+"F4.wireOp",EDGE,"E19.filletArc");var subQ2=sQuery(id+"F4.wireOp",EDGE,"E18.filletArc");var subQ3=sQuery(id+"F4.wireOp",EDGE,"E17.filletArc");var subQ4=sQuery(id+"F4.wireOp",EDGE,"E16.right");var subQ5=sQuery(id+"F4.wireOp",EDGE,"E16.left");var subQ6=sQuery(id+"F4.wireOp",EDGE,"E16.top");var subQ7=sQuery(id+"F4.wireOp",EDGE,"E16.bottom");var subQ8=sQuery(id+"F4.wireOp",EDGE,"E15.filletArc");var subQ9=sQuery(id+"F4.wireOp",EDGE,"E14.filletArc");var subQ10=sQuery(id+"F4.wireOp",EDGE,"E13.filletArc");var subQ11=sQuery(id+"F4.wireOp",EDGE,"E12.filletArc");var subQ12=sQuery(id+"F4.wireOp",EDGE,"E11.right");var subQ13=sQuery(id+"F4.wireOp",EDGE,"E11.left");var subQ14=sQuery(id+"F4.wireOp",EDGE,"E11.top");var subQ15=sQuery(id+"F4.wireOp",EDGE,"E11.bottom");var subQ16=sQuery(id+"F2.wireOp",EDGE,"E10.7");var subQ17=sQuery(id+"F2.wireOp",EDGE,"E10.6");var subQ18=sQuery(id+"F2.wireOp",EDGE,"E10.5");var subQ19=sQuery(id+"F2.wireOp",EDGE,"E10.4");var subQ20=sQuery(id+"F2.wireOp",EDGE,"E10.3");var subQ21=sQuery(id+"F2.wireOp",EDGE,"E10.2");var subQ22=sQuery(id+"F2.wireOp",EDGE,"E10.1");var subQ23=sQuery(id+"F2.wireOp",EDGE,"E10.0");var subQ24=sQuery(id+"F2.wireOp",EDGE,"E9.filletArc");var subQ25=sQuery(id+"F2.wireOp",EDGE,"E8.filletArc");var subQ26=sQuery(id+"F2.wireOp",EDGE,"E7.filletArc");var subQ27=sQuery(id+"F2.wireOp",EDGE,"E6.filletArc");var subQ28=sQuery(id+"F2.wireOp",EDGE,"E5.right");var subQ29=sQuery(id+"F2.wireOp",EDGE,"E5.left");var subQ30=sQuery(id+"F2.wireOp",EDGE,"E5.top");var subQ31=sQuery(id+"F2.wireOp",EDGE,"E5.bottom");Q1=makeQuery(id+"F24.boolean.opBoolean","MERGE",FACE,{"derivedFrom":[makeQuery(id+"F15.opBoolean","MERGE",FACE,{"derivedFrom":[makeQuery(id+"F3.opExtrude","CAP_FACE",FACE,{"disambiguationData":[OSD([subQ31,subQ30,subQ29,subQ28,subQ27,subQ26,subQ25,subQ24,subQ23,subQ22,subQ21,subQ20,subQ19,subQ18,subQ17,subQ16])],"isStart":true}),makeQuery(id+"F5.opExtrude","CAP_FACE",FACE,{"disambiguationData":[OSD([subQ15,subQ14,subQ13,subQ12,subQ11,subQ10,subQ9,subQ8,subQ7,subQ6,subQ5,subQ4,subQ3,subQ2,subQ1,subQ0])],"isStart":true})]}),makeQuery(id+"F22.boolean.opBoolean","MERGE",FACE,{"derivedFrom":[makeQuery(id+"F20.opShell","OFFSET_FACE",FACE,{"disambiguationData":[OSD([subQ31,subQ30,subQ29,subQ28,subQ27,subQ26,subQ25,subQ24,subQ23,subQ22,subQ21,subQ20,subQ19,subQ18,subQ17,subQ16,subQ15,subQ14,subQ13,subQ12,subQ11,subQ10,subQ9,subQ8,subQ7,subQ6,subQ5,subQ4,subQ3,subQ2,subQ1,subQ0])]}),makeQuery(id+"F22.opExtrude","CAP_FACE",FACE,{"disambiguationData":[OSD([sQuery(id+"F21.wireOp",EDGE,"E39"),sQuery(id+"F21.wireOp",EDGE,"E40"),sQuery(id+"F21.wireOp",EDGE,"E41"),sQuery(id+"F21.wireOp",EDGE,"E42")])],"isStart":false}),makeQuery(id+"F22.opExtrude","CAP_FACE",FACE,{"disambiguationData":[OSD([sQuery(id+"F21.wireOp",EDGE,"E46.MirrorCS"),sQuery(id+"F21.wireOp",EDGE,"E47.MirrorCS"),sQuery(id+"F21.wireOp",EDGE,"E49.MirrorCS"),sQuery(id+"F21.wireOp",EDGE,"E48.MirrorCS")])],"isStart":false}),makeQuery(id+"F22.opExtrude","CAP_FACE",FACE,{"disambiguationData":[OSD([sQuery(id+"F21.wireOp",EDGE,"E52.MirrorCS"),sQuery(id+"F21.wireOp",EDGE,"E53.MirrorCS"),sQuery(id+"F21.wireOp",EDGE,"E51.MirrorCS"),sQuery(id+"F21.wireOp",EDGE,"E54.MirrorCS")])],"isStart":false}),makeQuery(id+"F22.opExtrude","CAP_FACE",FACE,{"disambiguationData":[OSD([sQuery(id+"F21.wireOp",EDGE,"E55.MirrorCS"),sQuery(id+"F21.wireOp",EDGE,"E57.MirrorCS"),sQuery(id+"F21.wireOp",EDGE,"E59.MirrorCS"),sQuery(id+"F21.wireOp",EDGE,"E60.MirrorCS")])],"isStart":false})]}),makeQuery(id+"F24.opExtrude","CAP_FACE",FACE,{"disambiguationData":[OSD([sQuery(id+"F23.wireOp",EDGE,"E61"),sQuery(id+"F23.wireOp",EDGE,"E62"),sQuery(id+"F23.wireOp",EDGE,"E63"),sQuery(id+"F23.wireOp",EDGE,"E64"),sQuery(id+"F23.wireOp",EDGE,"E65"),sQuery(id+"F23.wireOp",EDGE,"E66"),sQuery(id+"F23.wireOp",EDGE,"E67"),sQuery(id+"F23.wireOp",EDGE,"E68")])],"isStart":false})]});}
            extrude(context, id + "F26", {"entities" : qUnion([Q0]), "operationType" : NewBodyOperationType.ADD, "endBound" : BoundingType.UP_TO_SURFACE, "depth" : 25 * mm, "endBoundEntityFace" : qUnion([Q1]), "offsetDistance" : 25 * mm});
        }
        {
            var Q0;
            {var subQ0=sQuery(id+"F23.wireOp",EDGE,"E68");var subQ1=sQuery(id+"F23.wireOp",EDGE,"E67");var subQ2=sQuery(id+"F23.wireOp",EDGE,"E66");var subQ3=sQuery(id+"F23.wireOp",EDGE,"E65");var subQ4=sQuery(id+"F23.wireOp",EDGE,"E64");var subQ5=sQuery(id+"F23.wireOp",EDGE,"E63");var subQ6=sQuery(id+"F23.wireOp",EDGE,"E62");var subQ7=sQuery(id+"F23.wireOp",EDGE,"E61");var subQ8=sQuery(id+"F21.wireOp",EDGE,"E60.MirrorCS");var subQ9=sQuery(id+"F21.wireOp",EDGE,"E59.MirrorCS");var subQ10=sQuery(id+"F21.wireOp",EDGE,"E57.MirrorCS");var subQ11=sQuery(id+"F21.wireOp",EDGE,"E55.MirrorCS");var subQ12=sQuery(id+"F21.wireOp",EDGE,"E54.MirrorCS");var subQ13=sQuery(id+"F21.wireOp",EDGE,"E51.MirrorCS");var subQ14=sQuery(id+"F21.wireOp",EDGE,"E53.MirrorCS");var subQ15=sQuery(id+"F21.wireOp",EDGE,"E52.MirrorCS");var subQ16=sQuery(id+"F21.wireOp",EDGE,"E48.MirrorCS");var subQ17=sQuery(id+"F21.wireOp",EDGE,"E49.MirrorCS");var subQ18=sQuery(id+"F21.wireOp",EDGE,"E47.MirrorCS");var subQ19=sQuery(id+"F21.wireOp",EDGE,"E46.MirrorCS");var subQ20=sQuery(id+"F21.wireOp",EDGE,"E42");var subQ21=sQuery(id+"F21.wireOp",EDGE,"E41");var subQ22=sQuery(id+"F21.wireOp",EDGE,"E40");var subQ23=sQuery(id+"F21.wireOp",EDGE,"E39");var subQ24=sQuery(id+"F4.wireOp",EDGE,"E20.filletArc");var subQ25=sQuery(id+"F4.wireOp",EDGE,"E19.filletArc");var subQ26=sQuery(id+"F4.wireOp",EDGE,"E18.filletArc");var subQ27=sQuery(id+"F4.wireOp",EDGE,"E17.filletArc");var subQ28=sQuery(id+"F4.wireOp",EDGE,"E16.right");var subQ29=sQuery(id+"F4.wireOp",EDGE,"E16.left");var subQ30=sQuery(id+"F4.wireOp",EDGE,"E16.top");var subQ31=sQuery(id+"F4.wireOp",EDGE,"E16.bottom");var subQ32=sQuery(id+"F4.wireOp",EDGE,"E15.filletArc");var subQ33=sQuery(id+"F4.wireOp",EDGE,"E14.filletArc");var subQ34=sQuery(id+"F4.wireOp",EDGE,"E13.filletArc");var subQ35=sQuery(id+"F4.wireOp",EDGE,"E12.filletArc");var subQ36=sQuery(id+"F4.wireOp",EDGE,"E11.right");var subQ37=sQuery(id+"F4.wireOp",EDGE,"E11.left");var subQ38=sQuery(id+"F4.wireOp",EDGE,"E11.top");var subQ39=sQuery(id+"F4.wireOp",EDGE,"E11.bottom");var subQ40=sQuery(id+"F2.wireOp",EDGE,"E10.7");var subQ41=sQuery(id+"F2.wireOp",EDGE,"E10.6");var subQ42=sQuery(id+"F2.wireOp",EDGE,"E10.5");var subQ43=sQuery(id+"F2.wireOp",EDGE,"E10.4");var subQ44=sQuery(id+"F2.wireOp",EDGE,"E10.3");var subQ45=sQuery(id+"F2.wireOp",EDGE,"E10.2");var subQ46=sQuery(id+"F2.wireOp",EDGE,"E10.1");var subQ47=sQuery(id+"F2.wireOp",EDGE,"E10.0");var subQ48=sQuery(id+"F2.wireOp",EDGE,"E9.filletArc");var subQ49=sQuery(id+"F2.wireOp",EDGE,"E8.filletArc");var subQ50=sQuery(id+"F2.wireOp",EDGE,"E7.filletArc");var subQ51=sQuery(id+"F2.wireOp",EDGE,"E6.filletArc");var subQ52=sQuery(id+"F2.wireOp",EDGE,"E5.right");var subQ53=sQuery(id+"F2.wireOp",EDGE,"E5.left");var subQ54=sQuery(id+"F2.wireOp",EDGE,"E5.top");var subQ55=sQuery(id+"F2.wireOp",EDGE,"E5.bottom");Q0=makeQuery(id+"F26.boolean.opBoolean","MERGE",FACE,{"derivedFrom":[makeQuery(id+"F24.boolean.opBoolean","MERGE",FACE,{"derivedFrom":[makeQuery(id+"F15.opBoolean","MERGE",FACE,{"derivedFrom":[makeQuery(id+"F3.opExtrude","CAP_FACE",FACE,{"disambiguationData":[OSD([subQ55,subQ54,subQ53,subQ52,subQ51,subQ50,subQ49,subQ48,subQ47,subQ46,subQ45,subQ44,subQ43,subQ42,subQ41,subQ40])],"isStart":true}),makeQuery(id+"F5.opExtrude","CAP_FACE",FACE,{"disambiguationData":[OSD([subQ39,subQ38,subQ37,subQ36,subQ35,subQ34,subQ33,subQ32,subQ31,subQ30,subQ29,subQ28,subQ27,subQ26,subQ25,subQ24])],"isStart":true})]}),makeQuery(id+"F22.boolean.opBoolean","MERGE",FACE,{"derivedFrom":[makeQuery(id+"F20.opShell","OFFSET_FACE",FACE,{"disambiguationData":[OSD([subQ55,subQ54,subQ53,subQ52,subQ51,subQ50,subQ49,subQ48,subQ47,subQ46,subQ45,subQ44,subQ43,subQ42,subQ41,subQ40,subQ39,subQ38,subQ37,subQ36,subQ35,subQ34,subQ33,subQ32,subQ31,subQ30,subQ29,subQ28,subQ27,subQ26,subQ25,subQ24])]}),makeQuery(id+"F22.opExtrude","CAP_FACE",FACE,{"disambiguationData":[OSD([subQ23,subQ22,subQ21,subQ20])],"isStart":false}),makeQuery(id+"F22.opExtrude","CAP_FACE",FACE,{"disambiguationData":[OSD([subQ19,subQ18,subQ17,subQ16])],"isStart":false}),makeQuery(id+"F22.opExtrude","CAP_FACE",FACE,{"disambiguationData":[OSD([subQ15,subQ14,subQ13,subQ12])],"isStart":false}),makeQuery(id+"F22.opExtrude","CAP_FACE",FACE,{"disambiguationData":[OSD([subQ11,subQ10,subQ9,subQ8])],"isStart":false})]}),makeQuery(id+"F24.opExtrude","CAP_FACE",FACE,{"disambiguationData":[OSD([subQ7,subQ6,subQ5,subQ4,subQ3,subQ2,subQ1,subQ0])],"isStart":false})]}),makeQuery(id+"F26.opExtrude","CAP_FACE",FACE,{"disambiguationData":[OSD([subQ55,subQ54,subQ53,subQ52,subQ51,subQ50,subQ49,subQ48,subQ47,subQ46,subQ45,subQ44,subQ43,subQ42,subQ41,subQ40,subQ39,subQ38,subQ37,subQ36,subQ35,subQ34,subQ33,subQ32,subQ31,subQ30,subQ29,subQ28,subQ27,subQ26,subQ25,subQ24,subQ23,subQ22,subQ21,subQ20,subQ19,subQ18,subQ17,subQ16,subQ15,subQ14,subQ13,subQ12,subQ11,subQ10,subQ9,subQ8,subQ7,subQ6,subQ5,subQ4,subQ3,subQ2,subQ1,subQ0])],"isStart":false})]});}
            var sketch = newSketch(context, id + "F27", { "sketchPlane" : qUnion([Q0])});
            skLineSegment(sketch, "E77", {"start": v(-79.5, 25.03) * mm, "end": v(-79.44, 25.1) * mm});
            skLineSegment(sketch, "E78", {"start": v(-79.44, 25.1) * mm, "end": v(-79.44, -25.1) * mm});
            skLineSegment(sketch, "E79", {"start": v(-79.5, -25.03) * mm, "end": v(-79.44, -25.1) * mm});
            skLineSegment(sketch, "E80", {"start": v(-79.5, -25.03) * mm, "end": v(-79.5, 25.03) * mm});
            skSolve(sketch);
        }
        {
            var Q0;
            Q0 = qSketchRegion(id + "F27", true);
            var Q1;
            {var subQ0=sQuery(id+"F4.wireOp",EDGE,"E19.filletArc");var subQ1=sQuery(id+"F4.wireOp",EDGE,"E17.filletArc");var subQ2=sQuery(id+"F4.wireOp",EDGE,"E16.left");var subQ3=sQuery(id+"F4.wireOp",EDGE,"E20.filletArc");var subQ4=sQuery(id+"F4.wireOp",EDGE,"E18.filletArc");var subQ5=sQuery(id+"F4.wireOp",EDGE,"E16.right");var subQ6=sQuery(id+"F4.wireOp",EDGE,"E16.top");var subQ7=sQuery(id+"F4.wireOp",EDGE,"E16.bottom");var subQ8=sQuery(id+"F4.wireOp",EDGE,"E15.filletArc");var subQ9=sQuery(id+"F4.wireOp",EDGE,"E14.filletArc");var subQ10=sQuery(id+"F4.wireOp",EDGE,"E13.filletArc");var subQ11=sQuery(id+"F4.wireOp",EDGE,"E12.filletArc");var subQ12=sQuery(id+"F4.wireOp",EDGE,"E11.right");var subQ13=sQuery(id+"F4.wireOp",EDGE,"E11.left");var subQ14=sQuery(id+"F4.wireOp",EDGE,"E11.top");var subQ15=sQuery(id+"F4.wireOp",EDGE,"E11.bottom");Q1=makeQuery(id+"F20.opShell","OFFSET_FACE",FACE,{"disambiguationData":[OSD([subQ15,subQ14,subQ13,subQ12,subQ11,subQ10,subQ9,subQ8,subQ7,subQ6,subQ2,subQ5,subQ1,subQ4,subQ0,subQ3]),TDD([makeQuery(id+"F15.opBoolean","SPLIT",FACE,{"disambiguationData":[TD([makeQuery(id+"F3.opExtrude","SWEPT_FACE",FACE,{"disambiguationData":[OSD([sQuery(id+"F2.wireOp",EDGE,"E5.left")])]})])],"derivedFrom":makeQuery(id+"F5.opExtrude","CAP_FACE",FACE,{"disambiguationData":[OSD([subQ15,subQ14,subQ13,subQ12,subQ11,subQ10,subQ9,subQ8,subQ7,subQ6,subQ2,subQ5,subQ1,subQ4,subQ0,subQ3])],"isStart":false})})])]});}
            extrude(context, id + "F28", {"entities" : qUnion([Q0]), "operationType" : NewBodyOperationType.ADD, "endBound" : BoundingType.UP_TO_SURFACE, "oppositeDirection" : true, "depth" : 25 * mm, "endBoundEntityFace" : qUnion([Q1]), "offsetDistance" : 25 * mm});
        }
        {
            var Q0;
            {var subQ0=sQuery(id+"F23.wireOp",EDGE,"E68");var subQ1=sQuery(id+"F23.wireOp",EDGE,"E67");var subQ2=sQuery(id+"F23.wireOp",EDGE,"E66");var subQ3=sQuery(id+"F23.wireOp",EDGE,"E65");var subQ4=sQuery(id+"F23.wireOp",EDGE,"E64");var subQ5=sQuery(id+"F23.wireOp",EDGE,"E63");var subQ6=sQuery(id+"F23.wireOp",EDGE,"E62");var subQ7=sQuery(id+"F23.wireOp",EDGE,"E61");var subQ8=sQuery(id+"F21.wireOp",EDGE,"E60.MirrorCS");var subQ9=sQuery(id+"F21.wireOp",EDGE,"E59.MirrorCS");var subQ10=sQuery(id+"F21.wireOp",EDGE,"E57.MirrorCS");var subQ11=sQuery(id+"F21.wireOp",EDGE,"E55.MirrorCS");var subQ12=sQuery(id+"F21.wireOp",EDGE,"E54.MirrorCS");var subQ13=sQuery(id+"F21.wireOp",EDGE,"E51.MirrorCS");var subQ14=sQuery(id+"F21.wireOp",EDGE,"E53.MirrorCS");var subQ15=sQuery(id+"F21.wireOp",EDGE,"E52.MirrorCS");var subQ16=sQuery(id+"F21.wireOp",EDGE,"E48.MirrorCS");var subQ17=sQuery(id+"F21.wireOp",EDGE,"E49.MirrorCS");var subQ18=sQuery(id+"F21.wireOp",EDGE,"E47.MirrorCS");var subQ19=sQuery(id+"F21.wireOp",EDGE,"E46.MirrorCS");var subQ20=sQuery(id+"F21.wireOp",EDGE,"E42");var subQ21=sQuery(id+"F21.wireOp",EDGE,"E41");var subQ22=sQuery(id+"F21.wireOp",EDGE,"E40");var subQ23=sQuery(id+"F21.wireOp",EDGE,"E39");var subQ24=sQuery(id+"F4.wireOp",EDGE,"E20.filletArc");var subQ25=sQuery(id+"F4.wireOp",EDGE,"E19.filletArc");var subQ26=sQuery(id+"F4.wireOp",EDGE,"E18.filletArc");var subQ27=sQuery(id+"F4.wireOp",EDGE,"E17.filletArc");var subQ28=sQuery(id+"F4.wireOp",EDGE,"E16.right");var subQ29=sQuery(id+"F4.wireOp",EDGE,"E16.left");var subQ30=sQuery(id+"F4.wireOp",EDGE,"E16.top");var subQ31=sQuery(id+"F4.wireOp",EDGE,"E16.bottom");var subQ32=sQuery(id+"F4.wireOp",EDGE,"E15.filletArc");var subQ33=sQuery(id+"F4.wireOp",EDGE,"E14.filletArc");var subQ34=sQuery(id+"F4.wireOp",EDGE,"E13.filletArc");var subQ35=sQuery(id+"F4.wireOp",EDGE,"E12.filletArc");var subQ36=sQuery(id+"F4.wireOp",EDGE,"E11.right");var subQ37=sQuery(id+"F4.wireOp",EDGE,"E11.left");var subQ38=sQuery(id+"F4.wireOp",EDGE,"E11.top");var subQ39=sQuery(id+"F4.wireOp",EDGE,"E11.bottom");var subQ40=sQuery(id+"F2.wireOp",EDGE,"E10.7");var subQ41=sQuery(id+"F2.wireOp",EDGE,"E10.6");var subQ42=sQuery(id+"F2.wireOp",EDGE,"E10.5");var subQ43=sQuery(id+"F2.wireOp",EDGE,"E10.4");var subQ44=sQuery(id+"F2.wireOp",EDGE,"E10.3");var subQ45=sQuery(id+"F2.wireOp",EDGE,"E10.2");var subQ46=sQuery(id+"F2.wireOp",EDGE,"E10.1");var subQ47=sQuery(id+"F2.wireOp",EDGE,"E10.0");var subQ48=sQuery(id+"F2.wireOp",EDGE,"E9.filletArc");var subQ49=sQuery(id+"F2.wireOp",EDGE,"E8.filletArc");var subQ50=sQuery(id+"F2.wireOp",EDGE,"E7.filletArc");var subQ51=sQuery(id+"F2.wireOp",EDGE,"E6.filletArc");var subQ52=sQuery(id+"F2.wireOp",EDGE,"E5.right");var subQ53=sQuery(id+"F2.wireOp",EDGE,"E5.left");var subQ54=sQuery(id+"F2.wireOp",EDGE,"E5.top");var subQ55=sQuery(id+"F2.wireOp",EDGE,"E5.bottom");Q0=makeQuery(id+"F28.boolean.opBoolean","MERGE",FACE,{"derivedFrom":[makeQuery(id+"F26.boolean.opBoolean","MERGE",FACE,{"derivedFrom":[makeQuery(id+"F24.boolean.opBoolean","MERGE",FACE,{"derivedFrom":[makeQuery(id+"F15.opBoolean","MERGE",FACE,{"derivedFrom":[makeQuery(id+"F3.opExtrude","CAP_FACE",FACE,{"disambiguationData":[OSD([subQ55,subQ54,subQ53,subQ52,subQ51,subQ50,subQ49,subQ48,subQ47,subQ46,subQ45,subQ44,subQ43,subQ42,subQ41,subQ40])],"isStart":true}),makeQuery(id+"F5.opExtrude","CAP_FACE",FACE,{"disambiguationData":[OSD([subQ39,subQ38,subQ37,subQ36,subQ35,subQ34,subQ33,subQ32,subQ31,subQ30,subQ29,subQ28,subQ27,subQ26,subQ25,subQ24])],"isStart":true})]}),makeQuery(id+"F22.boolean.opBoolean","MERGE",FACE,{"derivedFrom":[makeQuery(id+"F20.opShell","OFFSET_FACE",FACE,{"disambiguationData":[OSD([subQ55,subQ54,subQ53,subQ52,subQ51,subQ50,subQ49,subQ48,subQ47,subQ46,subQ45,subQ44,subQ43,subQ42,subQ41,subQ40,subQ39,subQ38,subQ37,subQ36,subQ35,subQ34,subQ33,subQ32,subQ31,subQ30,subQ29,subQ28,subQ27,subQ26,subQ25,subQ24])]}),makeQuery(id+"F22.opExtrude","CAP_FACE",FACE,{"disambiguationData":[OSD([subQ23,subQ22,subQ21,subQ20])],"isStart":false}),makeQuery(id+"F22.opExtrude","CAP_FACE",FACE,{"disambiguationData":[OSD([subQ19,subQ18,subQ17,subQ16])],"isStart":false}),makeQuery(id+"F22.opExtrude","CAP_FACE",FACE,{"disambiguationData":[OSD([subQ15,subQ14,subQ13,subQ12])],"isStart":false}),makeQuery(id+"F22.opExtrude","CAP_FACE",FACE,{"disambiguationData":[OSD([subQ11,subQ10,subQ9,subQ8])],"isStart":false})]}),makeQuery(id+"F24.opExtrude","CAP_FACE",FACE,{"disambiguationData":[OSD([subQ7,subQ6,subQ5,subQ4,subQ3,subQ2,subQ1,subQ0])],"isStart":false})]}),makeQuery(id+"F26.opExtrude","CAP_FACE",FACE,{"disambiguationData":[OSD([subQ55,subQ54,subQ53,subQ52,subQ51,subQ50,subQ49,subQ48,subQ47,subQ46,subQ45,subQ44,subQ43,subQ42,subQ41,subQ40,subQ39,subQ38,subQ37,subQ36,subQ35,subQ34,subQ33,subQ32,subQ31,subQ30,subQ29,subQ28,subQ27,subQ26,subQ25,subQ24,subQ23,subQ22,subQ21,subQ20,subQ19,subQ18,subQ17,subQ16,subQ15,subQ14,subQ13,subQ12,subQ11,subQ10,subQ9,subQ8,subQ7,subQ6,subQ5,subQ4,subQ3,subQ2,subQ1,subQ0])],"isStart":false})]}),makeQuery(id+"F28.opExtrude","CAP_FACE",FACE,{"disambiguationData":[OSD([sQuery(id+"F27.wireOp",EDGE,"E77"),sQuery(id+"F27.wireOp",EDGE,"E78"),sQuery(id+"F27.wireOp",EDGE,"E79"),sQuery(id+"F27.wireOp",EDGE,"E80")])],"isStart":true})]});}
            var sketch = newSketch(context, id + "F29", { "sketchPlane" : qUnion([Q0])});
            skPoint(sketch, "E81.end.orphan", {"position": v(0, 76.5) * mm});
            skPoint(sketch, "E81.start.orphan", {"position": v(0, -64) * mm});
            skLineSegment(sketch, "E82", {"start": v(0, 76.5) * mm, "end": v(0, 66.5) * mm});
            skLineSegment(sketch, "E83", {"start": v(79.44, 0) * mm, "end": v(89.5, 0) * mm});
            skPoint(sketch, "E84.end.orphan", {"position": v(76.94, 0) * mm});
            skLineSegment(sketch, "E85.bottom", {"start": v(92, -19.89) * mm, "end": v(76.94, -19.89) * mm});
            skLineSegment(sketch, "E85.top", {"start": v(92, 19.89) * mm, "end": v(76.94, 19.89) * mm});
            skLineSegment(sketch, "E85.left", {"start": v(92, -19.89) * mm, "end": v(92, 19.89) * mm});
            skLineSegment(sketch, "E85.right", {"start": v(76.94, -19.89) * mm, "end": v(76.94, 19.89) * mm});
            skPoint(sketch, "E85.middle", {"position": v(84.47, 0) * mm});
            skSolve(sketch);
        }
        {
            var Q0;
            Q0 = qSketchRegion(id + "F29", true);
            var Q1;
            {var subQ0=sQuery(id+"F2.wireOp",EDGE,"E10.3");var subQ1=sQuery(id+"F2.wireOp",EDGE,"E10.2");var subQ2=sQuery(id+"F2.wireOp",EDGE,"E9.filletArc");var subQ3=sQuery(id+"F2.wireOp",EDGE,"E8.filletArc");var subQ4=sQuery(id+"F2.wireOp",EDGE,"E7.filletArc");var subQ5=sQuery(id+"F2.wireOp",EDGE,"E10.1");var subQ6=sQuery(id+"F2.wireOp",EDGE,"E5.bottom");var subQ7=sQuery(id+"F2.wireOp",EDGE,"E5.right");var subQ8=sQuery(id+"F2.wireOp",EDGE,"E5.top");var subQ9=sQuery(id+"F2.wireOp",EDGE,"E5.left");var subQ10=sQuery(id+"F2.wireOp",EDGE,"E10.4");var subQ11=sQuery(id+"F2.wireOp",EDGE,"E10.5");var subQ12=sQuery(id+"F2.wireOp",EDGE,"E10.6");var subQ13=sQuery(id+"F2.wireOp",EDGE,"E10.7");var subQ14=sQuery(id+"F2.wireOp",EDGE,"E10.0");var subQ15=sQuery(id+"F2.wireOp",EDGE,"E6.filletArc");Q1=makeQuery(id+"F20.opShell","OFFSET_FACE",FACE,{"disambiguationData":[OSD([subQ6,subQ8,subQ9,subQ7,subQ15,subQ4,subQ3,subQ2,subQ14,subQ5,subQ1,subQ0,subQ10,subQ11,subQ12,subQ13]),TDD([makeQuery(id+"F11.boolean.opBoolean","SPLIT",FACE,{"disambiguationData":[TD([makeQuery(id+"F3.opExtrude","SWEPT_FACE",FACE,{"disambiguationData":[OSD([subQ8])]})])],"derivedFrom":makeQuery(id+"F3.opExtrude","CAP_FACE",FACE,{"disambiguationData":[OSD([subQ6,subQ8,subQ9,subQ7,subQ15,subQ4,subQ3,subQ2,subQ14,subQ5,subQ1,subQ0,subQ10,subQ11,subQ12,subQ13])],"isStart":false})})])]});}
            extrude(context, id + "F30", {"entities" : qUnion([Q0]), "operationType" : NewBodyOperationType.ADD, "endBound" : BoundingType.UP_TO_SURFACE, "oppositeDirection" : true, "depth" : 25 * mm, "endBoundEntityFace" : qUnion([Q1]), "offsetDistance" : 25 * mm});
        }
        {
            var Q0;
            {var subQ0=sQuery(id+"F23.wireOp",EDGE,"E68");var subQ1=sQuery(id+"F23.wireOp",EDGE,"E67");var subQ2=sQuery(id+"F23.wireOp",EDGE,"E66");var subQ3=sQuery(id+"F23.wireOp",EDGE,"E65");var subQ4=sQuery(id+"F23.wireOp",EDGE,"E64");var subQ5=sQuery(id+"F23.wireOp",EDGE,"E63");var subQ6=sQuery(id+"F23.wireOp",EDGE,"E62");var subQ7=sQuery(id+"F23.wireOp",EDGE,"E61");var subQ8=sQuery(id+"F21.wireOp",EDGE,"E60.MirrorCS");var subQ9=sQuery(id+"F21.wireOp",EDGE,"E59.MirrorCS");var subQ10=sQuery(id+"F21.wireOp",EDGE,"E57.MirrorCS");var subQ11=sQuery(id+"F21.wireOp",EDGE,"E55.MirrorCS");var subQ12=sQuery(id+"F21.wireOp",EDGE,"E54.MirrorCS");var subQ13=sQuery(id+"F21.wireOp",EDGE,"E51.MirrorCS");var subQ14=sQuery(id+"F21.wireOp",EDGE,"E53.MirrorCS");var subQ15=sQuery(id+"F21.wireOp",EDGE,"E52.MirrorCS");var subQ16=sQuery(id+"F21.wireOp",EDGE,"E48.MirrorCS");var subQ17=sQuery(id+"F21.wireOp",EDGE,"E49.MirrorCS");var subQ18=sQuery(id+"F21.wireOp",EDGE,"E47.MirrorCS");var subQ19=sQuery(id+"F21.wireOp",EDGE,"E46.MirrorCS");var subQ20=sQuery(id+"F21.wireOp",EDGE,"E42");var subQ21=sQuery(id+"F21.wireOp",EDGE,"E41");var subQ22=sQuery(id+"F21.wireOp",EDGE,"E40");var subQ23=sQuery(id+"F21.wireOp",EDGE,"E39");var subQ24=sQuery(id+"F4.wireOp",EDGE,"E20.filletArc");var subQ25=sQuery(id+"F4.wireOp",EDGE,"E19.filletArc");var subQ26=sQuery(id+"F4.wireOp",EDGE,"E18.filletArc");var subQ27=sQuery(id+"F4.wireOp",EDGE,"E17.filletArc");var subQ28=sQuery(id+"F4.wireOp",EDGE,"E16.right");var subQ29=sQuery(id+"F4.wireOp",EDGE,"E16.left");var subQ30=sQuery(id+"F4.wireOp",EDGE,"E16.top");var subQ31=sQuery(id+"F4.wireOp",EDGE,"E16.bottom");var subQ32=sQuery(id+"F4.wireOp",EDGE,"E15.filletArc");var subQ33=sQuery(id+"F4.wireOp",EDGE,"E14.filletArc");var subQ34=sQuery(id+"F4.wireOp",EDGE,"E13.filletArc");var subQ35=sQuery(id+"F4.wireOp",EDGE,"E12.filletArc");var subQ36=sQuery(id+"F4.wireOp",EDGE,"E11.right");var subQ37=sQuery(id+"F4.wireOp",EDGE,"E11.left");var subQ38=sQuery(id+"F4.wireOp",EDGE,"E11.top");var subQ39=sQuery(id+"F4.wireOp",EDGE,"E11.bottom");var subQ40=sQuery(id+"F2.wireOp",EDGE,"E10.7");var subQ41=sQuery(id+"F2.wireOp",EDGE,"E10.6");var subQ42=sQuery(id+"F2.wireOp",EDGE,"E10.5");var subQ43=sQuery(id+"F2.wireOp",EDGE,"E10.4");var subQ44=sQuery(id+"F2.wireOp",EDGE,"E10.3");var subQ45=sQuery(id+"F2.wireOp",EDGE,"E10.2");var subQ46=sQuery(id+"F2.wireOp",EDGE,"E10.1");var subQ47=sQuery(id+"F2.wireOp",EDGE,"E10.0");var subQ48=sQuery(id+"F2.wireOp",EDGE,"E9.filletArc");var subQ49=sQuery(id+"F2.wireOp",EDGE,"E8.filletArc");var subQ50=sQuery(id+"F2.wireOp",EDGE,"E7.filletArc");var subQ51=sQuery(id+"F2.wireOp",EDGE,"E6.filletArc");var subQ52=sQuery(id+"F2.wireOp",EDGE,"E5.right");var subQ53=sQuery(id+"F2.wireOp",EDGE,"E5.left");var subQ54=sQuery(id+"F2.wireOp",EDGE,"E5.top");var subQ55=sQuery(id+"F2.wireOp",EDGE,"E5.bottom");Q0=makeQuery(id+"F30.boolean.opBoolean","MERGE",FACE,{"derivedFrom":[makeQuery(id+"F28.boolean.opBoolean","MERGE",FACE,{"derivedFrom":[makeQuery(id+"F26.boolean.opBoolean","MERGE",FACE,{"derivedFrom":[makeQuery(id+"F24.boolean.opBoolean","MERGE",FACE,{"derivedFrom":[makeQuery(id+"F15.opBoolean","MERGE",FACE,{"derivedFrom":[makeQuery(id+"F3.opExtrude","CAP_FACE",FACE,{"disambiguationData":[OSD([subQ55,subQ54,subQ53,subQ52,subQ51,subQ50,subQ49,subQ48,subQ47,subQ46,subQ45,subQ44,subQ43,subQ42,subQ41,subQ40])],"isStart":true}),makeQuery(id+"F5.opExtrude","CAP_FACE",FACE,{"disambiguationData":[OSD([subQ39,subQ38,subQ37,subQ36,subQ35,subQ34,subQ33,subQ32,subQ31,subQ30,subQ29,subQ28,subQ27,subQ26,subQ25,subQ24])],"isStart":true})]}),makeQuery(id+"F22.boolean.opBoolean","MERGE",FACE,{"derivedFrom":[makeQuery(id+"F20.opShell","OFFSET_FACE",FACE,{"disambiguationData":[OSD([subQ55,subQ54,subQ53,subQ52,subQ51,subQ50,subQ49,subQ48,subQ47,subQ46,subQ45,subQ44,subQ43,subQ42,subQ41,subQ40,subQ39,subQ38,subQ37,subQ36,subQ35,subQ34,subQ33,subQ32,subQ31,subQ30,subQ29,subQ28,subQ27,subQ26,subQ25,subQ24])]}),makeQuery(id+"F22.opExtrude","CAP_FACE",FACE,{"disambiguationData":[OSD([subQ23,subQ22,subQ21,subQ20])],"isStart":false}),makeQuery(id+"F22.opExtrude","CAP_FACE",FACE,{"disambiguationData":[OSD([subQ19,subQ18,subQ17,subQ16])],"isStart":false}),makeQuery(id+"F22.opExtrude","CAP_FACE",FACE,{"disambiguationData":[OSD([subQ15,subQ14,subQ13,subQ12])],"isStart":false}),makeQuery(id+"F22.opExtrude","CAP_FACE",FACE,{"disambiguationData":[OSD([subQ11,subQ10,subQ9,subQ8])],"isStart":false})]}),makeQuery(id+"F24.opExtrude","CAP_FACE",FACE,{"disambiguationData":[OSD([subQ7,subQ6,subQ5,subQ4,subQ3,subQ2,subQ1,subQ0])],"isStart":false})]}),makeQuery(id+"F26.opExtrude","CAP_FACE",FACE,{"disambiguationData":[OSD([subQ55,subQ54,subQ53,subQ52,subQ51,subQ50,subQ49,subQ48,subQ47,subQ46,subQ45,subQ44,subQ43,subQ42,subQ41,subQ40,subQ39,subQ38,subQ37,subQ36,subQ35,subQ34,subQ33,subQ32,subQ31,subQ30,subQ29,subQ28,subQ27,subQ26,subQ25,subQ24,subQ23,subQ22,subQ21,subQ20,subQ19,subQ18,subQ17,subQ16,subQ15,subQ14,subQ13,subQ12,subQ11,subQ10,subQ9,subQ8,subQ7,subQ6,subQ5,subQ4,subQ3,subQ2,subQ1,subQ0])],"isStart":false})]}),makeQuery(id+"F28.opExtrude","CAP_FACE",FACE,{"disambiguationData":[OSD([sQuery(id+"F27.wireOp",EDGE,"E77"),sQuery(id+"F27.wireOp",EDGE,"E78"),sQuery(id+"F27.wireOp",EDGE,"E79"),sQuery(id+"F27.wireOp",EDGE,"E80")])],"isStart":true})]}),makeQuery(id+"F30.opExtrude","CAP_FACE",FACE,{"disambiguationData":[OSD([sQuery(id+"F29.wireOp",EDGE,"E85.bottom"),sQuery(id+"F29.wireOp",EDGE,"E85.top"),sQuery(id+"F29.wireOp",EDGE,"E85.left"),sQuery(id+"F29.wireOp",EDGE,"E85.right")])],"isStart":true})]});}
            var sketch = newSketch(context, id + "F31", { "sketchPlane" : qUnion([Q0])});
            skLineSegment(sketch, "E86", {"start": v(0, 66.5) * mm, "end": v(0, 76.5) * mm});
            skPoint(sketch, "E86.startSnap0", {"position": v(0, 64) * mm});
            skLineSegment(sketch, "E87.bottom", {"start": v(20.1, 64) * mm, "end": v(-20.1, 64) * mm});
            skLineSegment(sketch, "E87.top", {"start": v(20.1, 79) * mm, "end": v(-20.1, 79) * mm});
            skLineSegment(sketch, "E87.left", {"start": v(20.1, 64) * mm, "end": v(20.1, 79) * mm});
            skLineSegment(sketch, "E87.right", {"start": v(-20.1, 64) * mm, "end": v(-20.1, 79) * mm});
            skPoint(sketch, "E87.middle", {"position": v(0, 71.5) * mm});
            skSolve(sketch);
        }
        {
            var Q0;
            Q0 = qSketchRegion(id + "F31", true);
            var Q1;
            {var subQ0=sQuery(id+"F2.wireOp",EDGE,"E10.6");var subQ1=sQuery(id+"F2.wireOp",EDGE,"E10.3");var subQ3=sQuery(id+"F2.wireOp",EDGE,"E8.filletArc");var subQ4=sQuery(id+"F2.wireOp",EDGE,"E5.right");var subQ5=sQuery(id+"F2.wireOp",EDGE,"E10.7");var subQ6=sQuery(id+"F2.wireOp",EDGE,"E9.filletArc");var subQ8=sQuery(id+"F2.wireOp",EDGE,"E10.1");var subQ9=sQuery(id+"F2.wireOp",EDGE,"E10.5");var subQ10=sQuery(id+"F2.wireOp",EDGE,"E5.top");var subQ11=sQuery(id+"F2.wireOp",EDGE,"E5.left");var subQ12=sQuery(id+"F2.wireOp",EDGE,"E10.4");var subQ13=sQuery(id+"F2.wireOp",EDGE,"E10.2");var subQ14=sQuery(id+"F2.wireOp",EDGE,"E10.0");var subQ15=sQuery(id+"F2.wireOp",EDGE,"E7.filletArc");var subQ16=sQuery(id+"F2.wireOp",EDGE,"E6.filletArc");var subQ17=sQuery(id+"F2.wireOp",EDGE,"E5.bottom");var subQ19=makeQuery(id+"F3.opExtrude","CAP_FACE",FACE,{"disambiguationData":[OSD([subQ17,subQ10,subQ11,subQ4,subQ16,subQ15,subQ3,subQ6,subQ14,subQ8,subQ13,subQ1,subQ12,subQ9,subQ0,subQ5])],"isStart":false});Q1=makeQuery(id+"F30.boolean.opBoolean","SPLIT",FACE,{"disambiguationData":[TD([makeQuery(id+"F20.opShell","OFFSET_FACE",FACE,{"disambiguationData":[OSD([subQ10])]})])],"derivedFrom":makeQuery(id+"F20.opShell","OFFSET_FACE",FACE,{"disambiguationData":[OSD([subQ17,subQ10,subQ11,subQ4,subQ16,subQ15,subQ3,subQ6,subQ14,subQ8,subQ13,subQ1,subQ12,subQ9,subQ0,subQ5]),TDD([makeQuery(id+"F11.boolean.opBoolean","SPLIT",FACE,{"disambiguationData":[TD([makeQuery(id+"F3.opExtrude","SWEPT_FACE",FACE,{"disambiguationData":[OSD([subQ10])]})])],"derivedFrom":subQ19})])]})});}
            extrude(context, id + "F32", {"entities" : qUnion([Q0]), "operationType" : NewBodyOperationType.ADD, "endBound" : BoundingType.UP_TO_SURFACE, "oppositeDirection" : true, "depth" : 25 * mm, "endBoundEntityFace" : qUnion([Q1]), "offsetDistance" : 25 * mm});
        }
        {
            var Q0;
            {var subQ0=sQuery(id+"F2.wireOp",EDGE,"E6.filletArc");var subQ1=sQuery(id+"F2.wireOp",EDGE,"E5.left");var subQ2=sQuery(id+"F2.wireOp",EDGE,"E10.0");var subQ3=sQuery(id+"F2.wireOp",EDGE,"E5.bottom");var subQ4=sQuery(id+"F2.wireOp",EDGE,"E10.1");var subQ5=sQuery(id+"F2.wireOp",EDGE,"E10.2");Q0=makeQuery(id+"F11.boolean.opBoolean","SPLIT",FACE,{"disambiguationData":[TD([makeQuery(id+"F3.opExtrude","SWEPT_FACE",FACE,{"disambiguationData":[OSD([subQ0])]})])],"derivedFrom":makeQuery(id+"F3.opExtrude","CAP_FACE",FACE,{"disambiguationData":[OSD([subQ3,sQuery(id+"F2.wireOp",EDGE,"E5.top"),subQ1,sQuery(id+"F2.wireOp",EDGE,"E5.right"),subQ0,sQuery(id+"F2.wireOp",EDGE,"E7.filletArc"),sQuery(id+"F2.wireOp",EDGE,"E8.filletArc"),sQuery(id+"F2.wireOp",EDGE,"E9.filletArc"),subQ2,subQ4,subQ5,sQuery(id+"F2.wireOp",EDGE,"E10.3"),sQuery(id+"F2.wireOp",EDGE,"E10.4"),sQuery(id+"F2.wireOp",EDGE,"E10.5"),sQuery(id+"F2.wireOp",EDGE,"E10.6"),sQuery(id+"F2.wireOp",EDGE,"E10.7")])],"isStart":false})});}
            var sketch = newSketch(context, id + "F33", { "sketchPlane" : qUnion([Q0])});
            skLineSegment(sketch, "E88.bottom", {"start": v(52, -64) * mm, "end": v(-52, -64) * mm});
            skLineSegment(sketch, "E88.top", {"start": v(52, 64) * mm, "end": v(-52, 64) * mm});
            skLineSegment(sketch, "E88.left", {"start": v(77, -39) * mm, "end": v(77, 39) * mm});
            skLineSegment(sketch, "E88.right", {"start": v(-77, -39) * mm, "end": v(-77, 39) * mm});
            skPoint(sketch, "E88.middle", {"position": v(0, 0) * mm});
            skPoint(sketch, "E89.visualSharp", {"position": v(77, 64) * mm});
            skArc(sketch, "E89.filletArc", {"start": v(77, 39) * mm, "mid": v(69.68, 56.68) * mm, "end": v(52, 64) * mm});
            skPoint(sketch, "E90.visualSharp", {"position": v(-77, 64) * mm});
            skArc(sketch, "E90.filletArc", {"start": v(-52, 64) * mm, "mid": v(-69.68, 56.68) * mm, "end": v(-77, 39) * mm});
            skPoint(sketch, "E91.visualSharp", {"position": v(-77, -64) * mm});
            skArc(sketch, "E91.filletArc", {"start": v(-77, -39) * mm, "mid": v(-69.68, -56.68) * mm, "end": v(-52, -64) * mm});
            skPoint(sketch, "E92.visualSharp", {"position": v(77, -64) * mm});
            skArc(sketch, "E92.filletArc", {"start": v(52, -64) * mm, "mid": v(69.68, -56.68) * mm, "end": v(77, -39) * mm});
            skSolve(sketch);
        }
        {
            var Q0;
            Q0 = qSketchRegion(id + "F33", true);
            extrude(context, id + "F34", {"entities" : qUnion([Q0]), "operationType" : NewBodyOperationType.REMOVE, "oppositeDirection" : true, "depth" : 125 * mm, "offsetDistance" : 25 * mm});
        }
        {
            var Q0;
            {var subQ0=sQuery(id+"F10.wireOp",EDGE,"E28.top");Q0=makeQuery(id+"F17.boolean.opBoolean","MERGE",FACE,{"derivedFrom":[makeQuery(id+"F11.boolean.opBoolean","COPY",FACE,{"derivedFrom":makeQuery(id+"F11.opExtrude","SWEPT_FACE",FACE,{"disambiguationData":[OSD([subQ0])]})}),makeQuery(id+"F17.opExtrude","CAP_FACE",FACE,{"disambiguationData":[OSD([subQ0])],"isStart":false})]});}
            var sketch = newSketch(context, id + "F35", { "sketchPlane" : qUnion([Q0])});
            skLineSegment(sketch, "E93", {"start": v(23.76, 64) * mm, "end": v(-23.76, 64) * mm});
            skLineSegment(sketch, "E94", {"start": v(-23.76, 64) * mm, "end": v(-18.42, 69) * mm});
            skLineSegment(sketch, "E95", {"start": v(-18.42, 69) * mm, "end": v(-5.57, 69) * mm});
            skLineSegment(sketch, "E96", {"start": v(5.57, 69) * mm, "end": v(18.42, 69) * mm});
            skLineSegment(sketch, "E97", {"start": v(18.42, 69) * mm, "end": v(23.76, 64) * mm});
            skArc(sketch, "E98", {"start": v(12.63, 79) * mm, "mid": v(6.5, 75.83) * mm, "end": v(5.57, 69) * mm});
            skArc(sketch, "E99", {"start": v(-5.57, 69) * mm, "mid": v(-6.5, 75.83) * mm, "end": v(-12.63, 79) * mm});
            skLineSegment(sketch, "E100", {"start": v(12.63, 79) * mm, "end": v(-12.63, 79) * mm});
            skSolve(sketch);
        }
        {
            var Q0;
            Q0 = qSketchRegion(id + "F35", true);
            extrude(context, id + "F36", {"entities" : qUnion([Q0]), "operationType" : NewBodyOperationType.REMOVE, "oppositeDirection" : true, "depth" : 12 * mm, "offsetDistance" : 25 * mm});
        }
        {
            var Q0;
            {var subQ0=sQuery(id+"F8.wireOp",EDGE,"E26.top");Q0=makeQuery(id+"F19.boolean.opBoolean","MERGE",FACE,{"derivedFrom":[makeQuery(id+"F9.boolean.opBoolean","COPY",FACE,{"derivedFrom":makeQuery(id+"F9.opExtrude","SWEPT_FACE",FACE,{"disambiguationData":[OSD([subQ0])]})}),makeQuery(id+"F19.opExtrude","CAP_FACE",FACE,{"disambiguationData":[OSD([subQ0])],"isStart":false})]});}
            var sketch = newSketch(context, id + "F37", { "sketchPlane" : qUnion([Q0])});
            skLineSegment(sketch, "E101", {"start": v(-81.94, 5.58) * mm, "end": v(-81.94, 18.5) * mm});
            skLineSegment(sketch, "E102", {"start": v(-81.94, 18.5) * mm, "end": v(-77, 24.08) * mm});
            skLineSegment(sketch, "E103", {"start": v(-77, 24.08) * mm, "end": v(-77, -24.08) * mm});
            skLineSegment(sketch, "E104", {"start": v(-77, -24.08) * mm, "end": v(-81.94, -18.5) * mm});
            skLineSegment(sketch, "E105", {"start": v(-81.94, -18.5) * mm, "end": v(-81.94, -5.58) * mm});
            skArc(sketch, "E106", {"start": v(-81.94, -5.58) * mm, "mid": v(-88.8, -6.49) * mm, "end": v(-92, -12.63) * mm});
            skLineSegment(sketch, "E107", {"start": v(-92, -12.63) * mm, "end": v(-92, 12.63) * mm});
            skArc(sketch, "E108", {"start": v(-92, 12.63) * mm, "mid": v(-88.8, 6.49) * mm, "end": v(-81.94, 5.58) * mm});
            skSolve(sketch);
        }
        {
            var Q0;
            Q0 = qSketchRegion(id + "F37", true);
            extrude(context, id + "F38", {"entities" : qUnion([Q0]), "operationType" : NewBodyOperationType.REMOVE, "oppositeDirection" : true, "depth" : 11.9 * mm, "offsetDistance" : 25 * mm});
        }
    });
